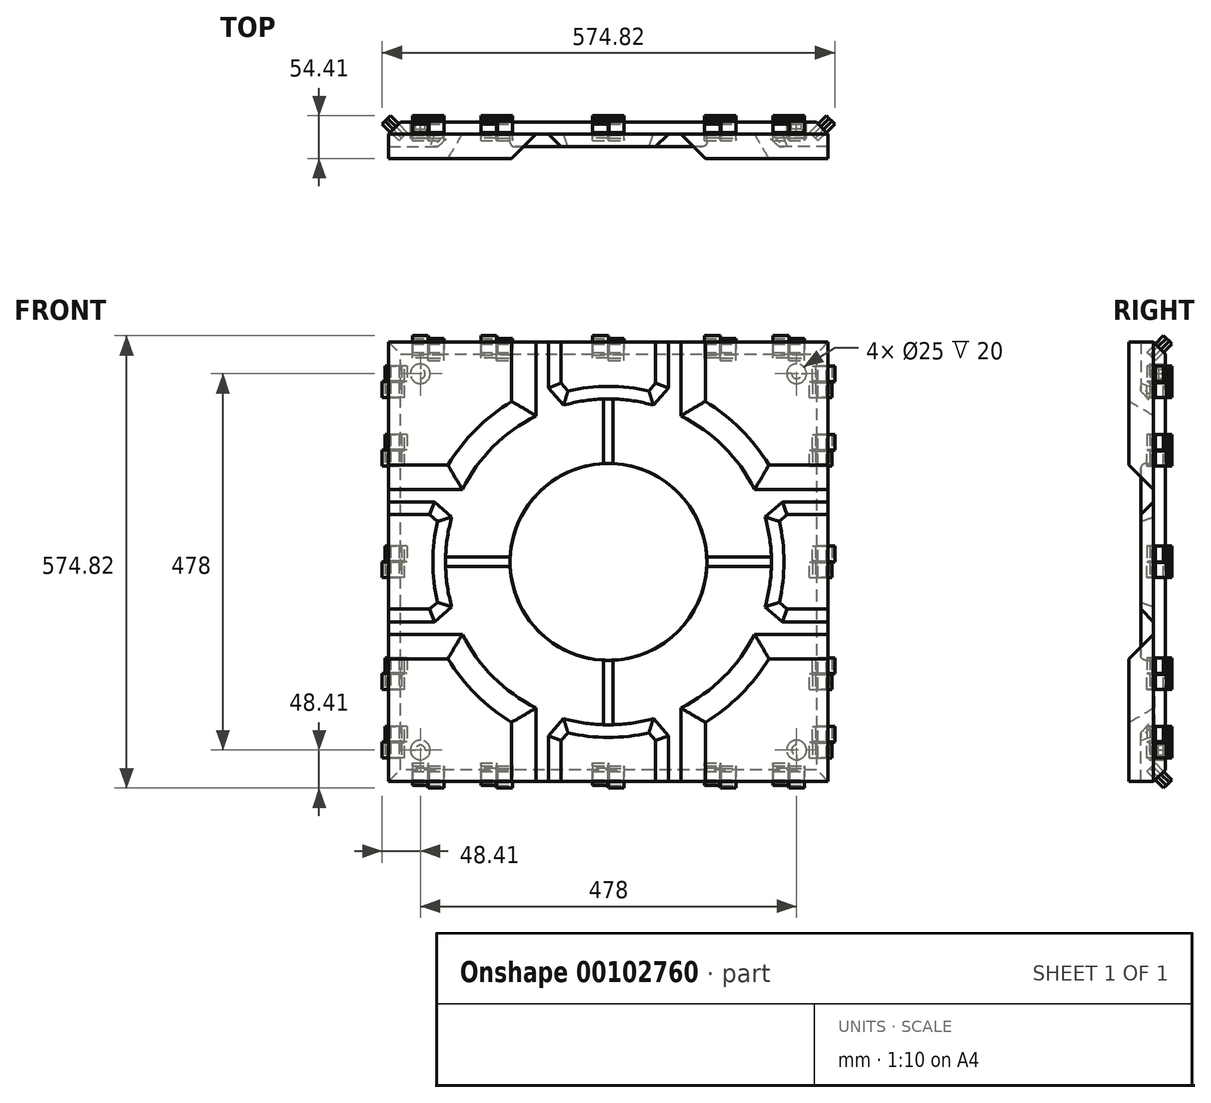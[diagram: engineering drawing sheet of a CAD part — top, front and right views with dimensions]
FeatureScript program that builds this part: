
annotation { "Feature Type Name" : "Feature", "Feature Type Description" : "" }
export const myFeature = defineFeature(function(context is Context, id is Id, definition is map)
    precondition{}
    {
        {
            var Q0;
            Q0=qCreatedBy(makeId("Front.planeOp"),FACE);
            var sketch = newSketch(context, id + "F0", { "sketchPlane" : qUnion([Q0])});
            skLineSegment(sketch, "E0.bottom", {"start": v(279, -279) * mm, "end": v(-279, -279) * mm});
            skLineSegment(sketch, "E0.top", {"start": v(279, 279) * mm, "end": v(-279, 279) * mm});
            skLineSegment(sketch, "E0.left", {"start": v(279, -279) * mm, "end": v(279, 279) * mm});
            skLineSegment(sketch, "E0.right", {"start": v(-279, -279) * mm, "end": v(-279, 279) * mm});
            skPoint(sketch, "E0.middle", {"position": v(0, 0) * mm});
            skCircle(sketch, "E1", {"center": v(0, 0) * mm, "radius": 125 * mm});
            skCircle(sketch, "E2", {"center": v(0, 0) * mm, "radius": 207 * mm});
            skLineSegment(sketch, "E3", {"start": v(-92, 279) * mm, "end": v(-92, 185.43) * mm});
            skLineSegment(sketch, "E4", {"start": v(-279, 92) * mm, "end": v(-185.43, 92) * mm});
            skLineSegment(sketch, "E5", {"start": v(92, 185.43) * mm, "end": v(92, 279) * mm});
            skLineSegment(sketch, "E6", {"start": v(185.43, 92) * mm, "end": v(279, 92) * mm});
            skLineSegment(sketch, "E7", {"start": v(92, -185.43) * mm, "end": v(92, -279) * mm});
            skLineSegment(sketch, "E8", {"start": v(-92, -185.43) * mm, "end": v(-92, -279) * mm});
            skLineSegment(sketch, "E9", {"start": v(-185.43, -92) * mm, "end": v(-279, -92) * mm});
            skLineSegment(sketch, "E10", {"start": v(185.43, -92) * mm, "end": v(279, -92) * mm});
            skLineSegment(sketch, "E11", {"start": v(-76, 279) * mm, "end": v(-76, 221) * mm});
            skLineSegment(sketch, "E12", {"start": v(76, 221) * mm, "end": v(76, 279) * mm});
            skLineSegment(sketch, "E13", {"start": v(-76, -221) * mm, "end": v(-76, -279) * mm});
            skLineSegment(sketch, "E14", {"start": v(76, -221) * mm, "end": v(76, -279) * mm});
            skLineSegment(sketch, "E15", {"start": v(-279, 76) * mm, "end": v(-221, 76) * mm});
            skLineSegment(sketch, "E16", {"start": v(-221, -76) * mm, "end": v(-279, -76) * mm});
            skLineSegment(sketch, "E17", {"start": v(221, 76) * mm, "end": v(279, 76) * mm});
            skLineSegment(sketch, "E18", {"start": v(221, -76) * mm, "end": v(279, -76) * mm});
            skLineSegment(sketch, "E19", {"start": v(-206.91, 6) * mm, "end": v(-124.86, 6) * mm});
            skLineSegment(sketch, "E20", {"start": v(-279, 0) * mm, "end": v(279, 0) * mm, "construction": true});
            skLineSegment(sketch, "E21", {"start": v(0, -279) * mm, "end": v(0, 279) * mm, "construction": true});
            skLineSegment(sketch, "E22", {"start": v(-206.91, -6) * mm, "end": v(-124.86, -6) * mm});
            skLineSegment(sketch, "E23", {"start": v(124.86, 6) * mm, "end": v(206.91, 6) * mm});
            skLineSegment(sketch, "E24", {"start": v(124.86, -6) * mm, "end": v(206.91, -6) * mm});
            skLineSegment(sketch, "E25", {"start": v(-6, 124.86) * mm, "end": v(-6, 206.91) * mm});
            skLineSegment(sketch, "E26", {"start": v(6, 206.91) * mm, "end": v(6, 124.86) * mm});
            skLineSegment(sketch, "E27", {"start": v(-6, -124.86) * mm, "end": v(-6, -206.91) * mm});
            skLineSegment(sketch, "E28", {"start": v(6, -124.86) * mm, "end": v(6, -206.91) * mm});
            skLineSegment(sketch, "E29", {"start": v(-199, 57) * mm, "end": v(-221, 76) * mm});
            skLineSegment(sketch, "E30", {"start": v(-199, -57) * mm, "end": v(-221, -76) * mm});
            skLineSegment(sketch, "E31", {"start": v(221, 76) * mm, "end": v(199, 57) * mm});
            skLineSegment(sketch, "E32", {"start": v(221, -76) * mm, "end": v(199, -57) * mm});
            skLineSegment(sketch, "E33", {"start": v(-76, 221) * mm, "end": v(-57, 199) * mm});
            skLineSegment(sketch, "E34", {"start": v(76, 221) * mm, "end": v(57, 199) * mm});
            skLineSegment(sketch, "E35", {"start": v(-57, -199) * mm, "end": v(-76, -221) * mm});
            skLineSegment(sketch, "E36", {"start": v(76, -221) * mm, "end": v(57, -199) * mm});
            skSolve(sketch);
        }
        {
            var Q0;
            Q0=qSketchRegion(id+"F0",true);
            var Q1;
            {var subQ3=sQuery(id+"F0.wireOp",EDGE,"E19");Q1=makeQuery(id+"F0.imprint","IMPRINT",FACE,{"disambiguationData":[TD([[makeQuery(id+"F0.imprint","IMPRINT",EDGE,{"derivedFrom":subQ3}),1.0]])]});}
            var Q2;
            {var subQ0=sQuery(id+"F0.wireOp",EDGE,"E25");Q2=makeQuery(id+"F0.imprint","IMPRINT",FACE,{"disambiguationData":[TD([[makeQuery(id+"F0.imprint","IMPRINT",EDGE,{"derivedFrom":subQ0}),-1.0]])]});}
            var Q3;
            {var subQ4=sQuery(id+"F0.wireOp",EDGE,"E23");Q3=makeQuery(id+"F0.imprint","IMPRINT",FACE,{"disambiguationData":[TD([[makeQuery(id+"F0.imprint","IMPRINT",EDGE,{"derivedFrom":subQ4}),1.0]])]});}
            var Q4;
            {var subQ0=sQuery(id+"F0.wireOp",EDGE,"E23");Q4=makeQuery(id+"F0.imprint","IMPRINT",FACE,{"disambiguationData":[TD([[makeQuery(id+"F0.imprint","IMPRINT",EDGE,{"derivedFrom":subQ0}),-1.0]])]});}
            var Q5;
            {var subQ5=sQuery(id+"F0.wireOp",EDGE,"E24");Q5=makeQuery(id+"F0.imprint","IMPRINT",FACE,{"disambiguationData":[TD([[makeQuery(id+"F0.imprint","IMPRINT",EDGE,{"derivedFrom":subQ5}),-1.0]])]});}
            var Q6;
            {var subQ0=sQuery(id+"F0.wireOp",EDGE,"E1");var subQ5=makeQuery(id+"F0.imprint","INTERSECT",VERTEX,{"derivedFrom":[subQ0,sQuery(id+"F0.wireOp",EDGE,"E23")]});Q6=makeQuery(id+"F0.imprint","IMPRINT",FACE,{"disambiguationData":[TD([[makeQuery(id+"F0.imprint","IMPRINT",EDGE,{"disambiguationData":[TD([[subQ5,-1.0]])],"derivedFrom":subQ0}),1.0]])]});}
            var Q7;
            {var subQ4=sQuery(id+"F0.wireOp",EDGE,"E22");Q7=makeQuery(id+"F0.imprint","IMPRINT",FACE,{"disambiguationData":[TD([[makeQuery(id+"F0.imprint","IMPRINT",EDGE,{"derivedFrom":subQ4}),-1.0]])]});}
            var Q8;
            {var subQ0=sQuery(id+"F0.wireOp",EDGE,"E27");Q8=makeQuery(id+"F0.imprint","IMPRINT",FACE,{"disambiguationData":[TD([[makeQuery(id+"F0.imprint","IMPRINT",EDGE,{"derivedFrom":subQ0}),1.0]])]});}
            var Q9;
            {var subQ0=sQuery(id+"F0.wireOp",EDGE,"E19");Q9=makeQuery(id+"F0.imprint","IMPRINT",FACE,{"disambiguationData":[TD([[makeQuery(id+"F0.imprint","IMPRINT",EDGE,{"derivedFrom":subQ0}),-1.0]])]});}
            extrude(context, id + "F1", {"entities" : qUnion([Q0, Q1, Q2, Q3, Q4, Q5, Q6, Q7, Q8, Q9]), "oppositeDirection" : true, "depth" : 15 * mm});
        }
        {
            var Q0;
            {var subQ0=sQuery(id+"F0.wireOp",EDGE,"E3");Q0=makeQuery(id+"F0.imprint","IMPRINT",FACE,{"disambiguationData":[TD([[makeQuery(id+"F0.imprint","IMPRINT",EDGE,{"derivedFrom":subQ0}),-1.0]])]});}
            var Q1;
            {var subQ0=sQuery(id+"F0.wireOp",EDGE,"E5");Q1=makeQuery(id+"F0.imprint","IMPRINT",FACE,{"disambiguationData":[TD([[makeQuery(id+"F0.imprint","IMPRINT",EDGE,{"derivedFrom":subQ0}),-1.0]])]});}
            var Q2;
            {var subQ0=sQuery(id+"F0.wireOp",EDGE,"E7");Q2=makeQuery(id+"F0.imprint","IMPRINT",FACE,{"disambiguationData":[TD([[makeQuery(id+"F0.imprint","IMPRINT",EDGE,{"derivedFrom":subQ0}),1.0]])]});}
            var Q3;
            {var subQ0=sQuery(id+"F0.wireOp",EDGE,"E8");Q3=makeQuery(id+"F0.imprint","IMPRINT",FACE,{"disambiguationData":[TD([[makeQuery(id+"F0.imprint","IMPRINT",EDGE,{"derivedFrom":subQ0}),-1.0]])]});}
            extrude(context, id + "F2", {"entities" : qUnion([Q0, Q1, Q2, Q3]), "operationType" : NewBodyOperationType.ADD, "depth" : 31 * mm});
        }
        {
            var Q0;
            {var subQ0=sQuery(id+"F0.wireOp",EDGE,"E2");Q0=makeQuery(id+"F2.opExtrude","CAP_EDGE",EDGE,{"disambiguationData":[OSD([subQ0]),TDD([makeQuery(id+"F0.imprint","IMPRINT",EDGE,{"disambiguationData":[TD([[makeQuery(id+"F0.imprint","INTERSECT",VERTEX,{"derivedFrom":[subQ0,sQuery(id+"F0.wireOp",EDGE,"E3")]}),-1.0]])],"derivedFrom":subQ0})])],"isStart":false});}
            var Q1;
            Q1=makeQuery(id+"F2.opExtrude","CAP_EDGE",EDGE,{"disambiguationData":[OSD([sQuery(id+"F0.wireOp",EDGE,"E4")])],"isStart":false});
            var Q2;
            Q2=makeQuery(id+"F2.opExtrude","CAP_EDGE",EDGE,{"disambiguationData":[OSD([sQuery(id+"F0.wireOp",EDGE,"E3")])],"isStart":false});
            var Q3;
            Q3=makeQuery(id+"F2.opExtrude","CAP_EDGE",EDGE,{"disambiguationData":[OSD([sQuery(id+"F0.wireOp",EDGE,"E5")])],"isStart":false});
            var Q4;
            {var subQ0=sQuery(id+"F0.wireOp",EDGE,"E2");Q4=makeQuery(id+"F2.opExtrude","CAP_EDGE",EDGE,{"disambiguationData":[OSD([subQ0]),TDD([makeQuery(id+"F0.imprint","IMPRINT",EDGE,{"disambiguationData":[TD([[makeQuery(id+"F0.imprint","INTERSECT",VERTEX,{"derivedFrom":[subQ0,sQuery(id+"F0.wireOp",EDGE,"E5")]}),1.0]])],"derivedFrom":subQ0})])],"isStart":false});}
            var Q5;
            Q5=makeQuery(id+"F2.opExtrude","CAP_EDGE",EDGE,{"disambiguationData":[OSD([sQuery(id+"F0.wireOp",EDGE,"E6")])],"isStart":false});
            var Q6;
            Q6=makeQuery(id+"F2.opExtrude","CAP_EDGE",EDGE,{"disambiguationData":[OSD([sQuery(id+"F0.wireOp",EDGE,"E10")])],"isStart":false});
            var Q7;
            {var subQ0=sQuery(id+"F0.wireOp",EDGE,"E2");Q7=makeQuery(id+"F2.opExtrude","CAP_EDGE",EDGE,{"disambiguationData":[OSD([subQ0]),TDD([makeQuery(id+"F0.imprint","IMPRINT",EDGE,{"disambiguationData":[TD([[makeQuery(id+"F0.imprint","INTERSECT",VERTEX,{"derivedFrom":[subQ0,sQuery(id+"F0.wireOp",EDGE,"E7")]}),-1.0]])],"derivedFrom":subQ0})])],"isStart":false});}
            var Q8;
            Q8=makeQuery(id+"F2.opExtrude","CAP_EDGE",EDGE,{"disambiguationData":[OSD([sQuery(id+"F0.wireOp",EDGE,"E7")])],"isStart":false});
            var Q9;
            Q9=makeQuery(id+"F2.opExtrude","CAP_EDGE",EDGE,{"disambiguationData":[OSD([sQuery(id+"F0.wireOp",EDGE,"E8")])],"isStart":false});
            var Q10;
            {var subQ0=sQuery(id+"F0.wireOp",EDGE,"E2");Q10=makeQuery(id+"F2.opExtrude","CAP_EDGE",EDGE,{"disambiguationData":[OSD([subQ0]),TDD([makeQuery(id+"F0.imprint","IMPRINT",EDGE,{"disambiguationData":[TD([[makeQuery(id+"F0.imprint","INTERSECT",VERTEX,{"derivedFrom":[subQ0,sQuery(id+"F0.wireOp",EDGE,"E8")]}),1.0]])],"derivedFrom":subQ0})])],"isStart":false});}
            var Q11;
            Q11=makeQuery(id+"F2.opExtrude","CAP_EDGE",EDGE,{"disambiguationData":[OSD([sQuery(id+"F0.wireOp",EDGE,"E9")])],"isStart":false});
            chamfer(context, id + "F3", {"entities" : qUnion([Q0, Q1, Q2, Q3, Q4, Q5, Q6, Q7, Q8, Q9, Q10, Q11]), "width" : 31 * mm, "tangentPropagation" : true});
        }
        {
            var Q0;
            {var subQ5=sQuery(id+"F0.wireOp",EDGE,"E15");Q0=makeQuery(id+"F0.imprint","IMPRINT",FACE,{"disambiguationData":[TD([[makeQuery(id+"F0.imprint","IMPRINT",EDGE,{"derivedFrom":subQ5}),-1.0]])]});}
            var Q1;
            {var subQ3=sQuery(id+"F0.wireOp",EDGE,"E11");Q1=makeQuery(id+"F0.imprint","IMPRINT",FACE,{"disambiguationData":[TD([[makeQuery(id+"F0.imprint","IMPRINT",EDGE,{"derivedFrom":subQ3}),1.0]])]});}
            var Q2;
            {var subQ0=sQuery(id+"F0.wireOp",EDGE,"E1");var subQ5=makeQuery(id+"F0.imprint","INTERSECT",VERTEX,{"derivedFrom":[subQ0,sQuery(id+"F0.wireOp",EDGE,"E23")]});Q2=makeQuery(id+"F0.imprint","IMPRINT",FACE,{"disambiguationData":[TD([[makeQuery(id+"F0.imprint","IMPRINT",EDGE,{"disambiguationData":[TD([[subQ5,-1.0]])],"derivedFrom":subQ0}),1.0]])]});}
            var Q3;
            {var subQ5=sQuery(id+"F0.wireOp",EDGE,"E17");Q3=makeQuery(id+"F0.imprint","IMPRINT",FACE,{"disambiguationData":[TD([[makeQuery(id+"F0.imprint","IMPRINT",EDGE,{"derivedFrom":subQ5}),-1.0]])]});}
            var Q4;
            {var subQ6=sQuery(id+"F0.wireOp",EDGE,"E13");Q4=makeQuery(id+"F0.imprint","IMPRINT",FACE,{"disambiguationData":[TD([[makeQuery(id+"F0.imprint","IMPRINT",EDGE,{"derivedFrom":subQ6}),1.0]])]});}
            extrude(context, id + "F4", {"entities" : qUnion([Q0, Q1, Q2, Q3, Q4]), "operationType" : NewBodyOperationType.ADD, "depth" : 16 * mm});
        }
        {
            var Q0;
            Q0=makeQuery(id+"F4.opExtrude","CAP_EDGE",EDGE,{"disambiguationData":[OSD([sQuery(id+"F0.wireOp",EDGE,"E15")])],"isStart":false});
            var Q1;
            Q1=makeQuery(id+"F4.opExtrude","CAP_EDGE",EDGE,{"disambiguationData":[OSD([sQuery(id+"F0.wireOp",EDGE,"E29")])],"isStart":false});
            var Q2;
            {var subQ0=sQuery(id+"F0.wireOp",EDGE,"E2");var subQ1=makeQuery(id+"F0.imprint","INTERSECT",VERTEX,{"derivedFrom":[subQ0,sQuery(id+"F0.wireOp",EDGE,"E22")]});var subQ2=makeQuery(id+"F0.imprint","INTERSECT",VERTEX,{"derivedFrom":[subQ0,sQuery(id+"F0.wireOp",EDGE,"E19")]});Q2=makeQuery(id+"F4.opExtrude","CAP_EDGE",EDGE,{"disambiguationData":[OSD([subQ0]),TDD([makeQuery(id+"F0.imprint","IMPRINT",EDGE,{"disambiguationData":[TD([[subQ2,1.0]])],"derivedFrom":subQ0}),makeQuery(id+"F0.imprint","IMPRINT",EDGE,{"disambiguationData":[TD([[subQ2,-1.0]])],"derivedFrom":subQ0}),makeQuery(id+"F0.imprint","IMPRINT",EDGE,{"disambiguationData":[TD([[subQ1,-1.0]])],"derivedFrom":subQ0})])],"isStart":false});}
            var Q3;
            Q3=makeQuery(id+"F4.opExtrude","CAP_EDGE",EDGE,{"disambiguationData":[OSD([sQuery(id+"F0.wireOp",EDGE,"E30")])],"isStart":false});
            var Q4;
            Q4=makeQuery(id+"F4.opExtrude","CAP_EDGE",EDGE,{"disambiguationData":[OSD([sQuery(id+"F0.wireOp",EDGE,"E16")])],"isStart":false});
            var Q5;
            Q5=makeQuery(id+"F4.opExtrude","CAP_EDGE",EDGE,{"disambiguationData":[OSD([sQuery(id+"F0.wireOp",EDGE,"E13")])],"isStart":false});
            var Q6;
            Q6=makeQuery(id+"F4.opExtrude","CAP_EDGE",EDGE,{"disambiguationData":[OSD([sQuery(id+"F0.wireOp",EDGE,"E35")])],"isStart":false});
            var Q7;
            {var subQ0=sQuery(id+"F0.wireOp",EDGE,"E2");var subQ1=makeQuery(id+"F0.imprint","INTERSECT",VERTEX,{"derivedFrom":[subQ0,sQuery(id+"F0.wireOp",EDGE,"E28")]});var subQ2=makeQuery(id+"F0.imprint","INTERSECT",VERTEX,{"derivedFrom":[subQ0,sQuery(id+"F0.wireOp",EDGE,"E27")]});Q7=makeQuery(id+"F4.opExtrude","CAP_EDGE",EDGE,{"disambiguationData":[OSD([subQ0]),TDD([makeQuery(id+"F0.imprint","IMPRINT",EDGE,{"disambiguationData":[TD([[subQ2,1.0]])],"derivedFrom":subQ0}),makeQuery(id+"F0.imprint","IMPRINT",EDGE,{"disambiguationData":[TD([[subQ2,-1.0]])],"derivedFrom":subQ0}),makeQuery(id+"F0.imprint","IMPRINT",EDGE,{"disambiguationData":[TD([[subQ1,-1.0]])],"derivedFrom":subQ0})])],"isStart":false});}
            var Q8;
            Q8=makeQuery(id+"F4.opExtrude","CAP_EDGE",EDGE,{"disambiguationData":[OSD([sQuery(id+"F0.wireOp",EDGE,"E36")])],"isStart":false});
            var Q9;
            Q9=makeQuery(id+"F4.opExtrude","CAP_EDGE",EDGE,{"disambiguationData":[OSD([sQuery(id+"F0.wireOp",EDGE,"E14")])],"isStart":false});
            var Q10;
            Q10=makeQuery(id+"F4.opExtrude","CAP_EDGE",EDGE,{"disambiguationData":[OSD([sQuery(id+"F0.wireOp",EDGE,"E18")])],"isStart":false});
            var Q11;
            Q11=makeQuery(id+"F4.opExtrude","CAP_EDGE",EDGE,{"disambiguationData":[OSD([sQuery(id+"F0.wireOp",EDGE,"E32")])],"isStart":false});
            var Q12;
            {var subQ0=sQuery(id+"F0.wireOp",EDGE,"E2");var subQ1=makeQuery(id+"F0.imprint","INTERSECT",VERTEX,{"derivedFrom":[subQ0,sQuery(id+"F0.wireOp",EDGE,"E23")]});var subQ2=makeQuery(id+"F0.imprint","INTERSECT",VERTEX,{"derivedFrom":[subQ0,sQuery(id+"F0.wireOp",EDGE,"E24")]});Q12=makeQuery(id+"F4.opExtrude","CAP_EDGE",EDGE,{"disambiguationData":[OSD([subQ0]),TDD([makeQuery(id+"F0.imprint","IMPRINT",EDGE,{"disambiguationData":[TD([[subQ1,-1.0]])],"derivedFrom":subQ0}),makeQuery(id+"F0.imprint","IMPRINT",EDGE,{"disambiguationData":[TD([[subQ2,1.0]])],"derivedFrom":subQ0}),makeQuery(id+"F0.imprint","IMPRINT",EDGE,{"disambiguationData":[TD([[subQ1,1.0]])],"derivedFrom":subQ0})])],"isStart":false});}
            var Q13;
            Q13=makeQuery(id+"F4.opExtrude","CAP_EDGE",EDGE,{"disambiguationData":[OSD([sQuery(id+"F0.wireOp",EDGE,"E31")])],"isStart":false});
            var Q14;
            Q14=makeQuery(id+"F4.opExtrude","CAP_EDGE",EDGE,{"disambiguationData":[OSD([sQuery(id+"F0.wireOp",EDGE,"E17")])],"isStart":false});
            var Q15;
            Q15=makeQuery(id+"F4.opExtrude","CAP_EDGE",EDGE,{"disambiguationData":[OSD([sQuery(id+"F0.wireOp",EDGE,"E12")])],"isStart":false});
            var Q16;
            Q16=makeQuery(id+"F4.opExtrude","CAP_EDGE",EDGE,{"disambiguationData":[OSD([sQuery(id+"F0.wireOp",EDGE,"E34")])],"isStart":false});
            var Q17;
            {var subQ0=sQuery(id+"F0.wireOp",EDGE,"E2");var subQ1=makeQuery(id+"F0.imprint","INTERSECT",VERTEX,{"derivedFrom":[subQ0,sQuery(id+"F0.wireOp",EDGE,"E25")]});var subQ2=makeQuery(id+"F0.imprint","INTERSECT",VERTEX,{"derivedFrom":[subQ0,sQuery(id+"F0.wireOp",EDGE,"E26")]});Q17=makeQuery(id+"F4.opExtrude","CAP_EDGE",EDGE,{"disambiguationData":[OSD([subQ0]),TDD([makeQuery(id+"F0.imprint","IMPRINT",EDGE,{"disambiguationData":[TD([[subQ2,1.0]])],"derivedFrom":subQ0}),makeQuery(id+"F0.imprint","IMPRINT",EDGE,{"disambiguationData":[TD([[subQ1,1.0]])],"derivedFrom":subQ0}),makeQuery(id+"F0.imprint","IMPRINT",EDGE,{"disambiguationData":[TD([[subQ1,-1.0]])],"derivedFrom":subQ0})])],"isStart":false});}
            var Q18;
            Q18=makeQuery(id+"F4.opExtrude","CAP_EDGE",EDGE,{"disambiguationData":[OSD([sQuery(id+"F0.wireOp",EDGE,"E33")])],"isStart":false});
            var Q19;
            Q19=makeQuery(id+"F4.opExtrude","CAP_EDGE",EDGE,{"disambiguationData":[OSD([sQuery(id+"F0.wireOp",EDGE,"E11")])],"isStart":false});
            chamfer(context, id + "F5", {"entities" : qUnion([Q0, Q1, Q2, Q3, Q4, Q5, Q6, Q7, Q8, Q9, Q10, Q11, Q12, Q13, Q14, Q15, Q16, Q17, Q18, Q19]), "width" : 16 * mm, "tangentPropagation" : true});
        }
        {
            var Q0;
            Q0=makeQuery(id+"F4.opExtrude","CAP_EDGE",EDGE,{"disambiguationData":[OSD([sQuery(id+"F0.wireOp",EDGE,"E1")])],"isStart":false});
            fillet(context, id + "F6", {"entities" : qUnion([Q0]), "radius" : 6 * mm, "tangentPropagation" : true, "allowEdgeOverflow" : false});
        }
        {
            var Q0;
            Q0=makeQuery(id+"F1.opExtrude","CAP_FACE",FACE,{"disambiguationData":[OSD([sQuery(id+"F0.wireOp",EDGE,"E0.bottom"),sQuery(id+"F0.wireOp",EDGE,"E0.top"),sQuery(id+"F0.wireOp",EDGE,"E0.left"),sQuery(id+"F0.wireOp",EDGE,"E0.right")])],"isStart":false});
            chamfer(context, id + "F7", {"entities" : qUnion([Q0]), "width" : 15 * mm, "tangentPropagation" : true});
        }
        {
            var Q0;
            {var subQ0=sQuery(id+"F0.wireOp",EDGE,"E19");Q0=makeQuery(id+"F0.imprint","IMPRINT",FACE,{"disambiguationData":[TD([[makeQuery(id+"F0.imprint","IMPRINT",EDGE,{"derivedFrom":subQ0}),-1.0]])]});}
            var Q1;
            {var subQ0=sQuery(id+"F0.wireOp",EDGE,"E25");Q1=makeQuery(id+"F0.imprint","IMPRINT",FACE,{"disambiguationData":[TD([[makeQuery(id+"F0.imprint","IMPRINT",EDGE,{"derivedFrom":subQ0}),-1.0]])]});}
            var Q2;
            {var subQ0=sQuery(id+"F0.wireOp",EDGE,"E23");Q2=makeQuery(id+"F0.imprint","IMPRINT",FACE,{"disambiguationData":[TD([[makeQuery(id+"F0.imprint","IMPRINT",EDGE,{"derivedFrom":subQ0}),-1.0]])]});}
            var Q3;
            {var subQ0=sQuery(id+"F0.wireOp",EDGE,"E27");Q3=makeQuery(id+"F0.imprint","IMPRINT",FACE,{"disambiguationData":[TD([[makeQuery(id+"F0.imprint","IMPRINT",EDGE,{"derivedFrom":subQ0}),1.0]])]});}
            extrude(context, id + "F8", {"entities" : qUnion([Q0, Q1, Q2, Q3]), "operationType" : NewBodyOperationType.REMOVE, "oppositeDirection" : true, "depth" : 1 * mm});
        }
        {
            var Q0;
            Q0=makeQuery(id+"F7.opChamfer","BLEND_FACE",FACE,{"disambiguationData":[OSD([sQuery(id+"F0.wireOp",EDGE,"E0.right")])]});
            var sketch = newSketch(context, id + "F9", { "sketchPlane" : qUnion([Q0])});
            skLineSegment(sketch, "E37.0", {"start": v(176.07, -264) * mm, "end": v(176.07, 264) * mm});
            skLineSegment(sketch, "E38.0", {"start": v(197.28, 76) * mm, "end": v(197.28, -76) * mm});
            skLineSegment(sketch, "E39.0", {"start": v(197.28, -92) * mm, "end": v(197.28, -279) * mm});
            skLineSegment(sketch, "E40.0", {"start": v(197.28, -92) * mm, "end": v(197.28, -76) * mm});
            skLineSegment(sketch, "E41.0", {"start": v(197.28, 76) * mm, "end": v(197.28, 92) * mm});
            skLineSegment(sketch, "E41.1", {"start": v(197.28, 279) * mm, "end": v(197.28, 92) * mm});
            skLineSegment(sketch, "E41.2", {"start": v(197.28, 279) * mm, "end": v(176.07, 264) * mm});
            skLineSegment(sketch, "E41.3", {"start": v(176.07, -264) * mm, "end": v(197.28, -279) * mm});
            skLineSegment(sketch, "E42", {"start": v(176.07, -263.86) * mm, "end": v(197.28, -263.86) * mm, "construction": true});
            skLineSegment(sketch, "E43", {"start": v(186.68, 267.3) * mm, "end": v(186.68, -263.86) * mm, "construction": true});
            skPoint(sketch, "E44.middle", {"position": v(186.68, 229) * mm});
            skLineSegment(sketch, "E45.bottom", {"start": v(179.18, 249) * mm, "end": v(194.18, 249) * mm});
            skLineSegment(sketch, "E45.top", {"start": v(179.18, 209) * mm, "end": v(194.18, 209) * mm});
            skLineSegment(sketch, "E45.left", {"start": v(179.18, 249) * mm, "end": v(179.18, 209) * mm});
            skLineSegment(sketch, "E45.right", {"start": v(194.18, 249) * mm, "end": v(194.18, 209) * mm});
            skLineSegment(sketch, "E46.MirrorCS", {"start": v(189.18, 249) * mm, "end": v(189.18, 230) * mm});
            skLineSegment(sketch, "E47", {"start": v(184.18, 209) * mm, "end": v(184.18, 228) * mm});
            skLineSegment(sketch, "E48.trimOffspring", {"start": v(184.18, 230) * mm, "end": v(184.18, 249) * mm});
            skLineSegment(sketch, "E49.trimOffspring", {"start": v(189.18, 228) * mm, "end": v(189.18, 209) * mm});
            skLineSegment(sketch, "E50", {"start": v(179.18, 229) * mm, "end": v(184.18, 230) * mm});
            skLineSegment(sketch, "E51", {"start": v(189.18, 230) * mm, "end": v(194.18, 229) * mm});
            skLineSegment(sketch, "E52", {"start": v(184.18, 228) * mm, "end": v(189.18, 228) * mm});
            skPoint(sketch, "E53.middle", {"position": v(186.68, 142) * mm});
            skLineSegment(sketch, "E54.bottom", {"start": v(179.18, 162) * mm, "end": v(194.18, 162) * mm});
            skLineSegment(sketch, "E54.top", {"start": v(179.18, 122) * mm, "end": v(194.18, 122) * mm});
            skLineSegment(sketch, "E54.left", {"start": v(179.18, 162) * mm, "end": v(179.18, 122) * mm});
            skLineSegment(sketch, "E54.right", {"start": v(194.18, 162) * mm, "end": v(194.18, 122) * mm});
            skLineSegment(sketch, "E55.MirrorCS", {"start": v(189.18, 162) * mm, "end": v(189.18, 143) * mm});
            skLineSegment(sketch, "E56", {"start": v(184.18, 122) * mm, "end": v(184.18, 141) * mm});
            skLineSegment(sketch, "E57.trimOffspring", {"start": v(184.18, 143) * mm, "end": v(184.18, 162) * mm});
            skLineSegment(sketch, "E58.trimOffspring", {"start": v(189.18, 141) * mm, "end": v(189.18, 122) * mm});
            skLineSegment(sketch, "E59", {"start": v(179.18, 142) * mm, "end": v(184.18, 143) * mm});
            skLineSegment(sketch, "E60", {"start": v(189.18, 143) * mm, "end": v(194.18, 142) * mm});
            skLineSegment(sketch, "E61", {"start": v(184.18, 141) * mm, "end": v(189.18, 141) * mm});
            skPoint(sketch, "E62.middle", {"position": v(186.68, 0) * mm});
            skLineSegment(sketch, "E63.bottom", {"start": v(179.18, 20) * mm, "end": v(194.18, 20) * mm});
            skLineSegment(sketch, "E63.top", {"start": v(179.18, -20) * mm, "end": v(194.18, -20) * mm});
            skLineSegment(sketch, "E63.left", {"start": v(179.18, 20) * mm, "end": v(179.18, -20) * mm});
            skLineSegment(sketch, "E63.right", {"start": v(194.18, 20) * mm, "end": v(194.18, -20) * mm});
            skLineSegment(sketch, "E64.MirrorCS", {"start": v(189.18, 20) * mm, "end": v(189.18, 1) * mm});
            skLineSegment(sketch, "E65", {"start": v(184.18, -20) * mm, "end": v(184.18, -1) * mm});
            skLineSegment(sketch, "E66.trimOffspring", {"start": v(184.18, 1) * mm, "end": v(184.18, 20) * mm});
            skLineSegment(sketch, "E67.trimOffspring", {"start": v(189.18, -1) * mm, "end": v(189.18, -20) * mm});
            skLineSegment(sketch, "E68", {"start": v(179.18, 0) * mm, "end": v(184.18, 1) * mm});
            skLineSegment(sketch, "E69", {"start": v(189.18, 1) * mm, "end": v(194.18, 0) * mm});
            skLineSegment(sketch, "E70", {"start": v(184.18, -1) * mm, "end": v(189.18, -1) * mm});
            skPoint(sketch, "E71.middle", {"position": v(186.68, -229) * mm});
            skLineSegment(sketch, "E72.bottom", {"start": v(179.18, -209) * mm, "end": v(194.18, -209) * mm});
            skLineSegment(sketch, "E72.top", {"start": v(179.18, -249) * mm, "end": v(194.18, -249) * mm});
            skLineSegment(sketch, "E72.left", {"start": v(179.18, -209) * mm, "end": v(179.18, -249) * mm});
            skLineSegment(sketch, "E72.right", {"start": v(194.18, -209) * mm, "end": v(194.18, -249) * mm});
            skLineSegment(sketch, "E73.MirrorCS", {"start": v(189.18, -209) * mm, "end": v(189.18, -228) * mm});
            skLineSegment(sketch, "E74", {"start": v(184.18, -249) * mm, "end": v(184.18, -230) * mm});
            skLineSegment(sketch, "E75.trimOffspring", {"start": v(184.18, -228) * mm, "end": v(184.18, -209) * mm});
            skLineSegment(sketch, "E76.trimOffspring", {"start": v(189.18, -230) * mm, "end": v(189.18, -249) * mm});
            skLineSegment(sketch, "E77", {"start": v(179.18, -229) * mm, "end": v(184.18, -228) * mm});
            skLineSegment(sketch, "E78", {"start": v(189.18, -228) * mm, "end": v(194.18, -229) * mm});
            skLineSegment(sketch, "E79", {"start": v(184.18, -230) * mm, "end": v(189.18, -230) * mm});
            skPoint(sketch, "E80.middle", {"position": v(186.68, -142) * mm});
            skLineSegment(sketch, "E81.bottom", {"start": v(179.18, -122) * mm, "end": v(194.18, -122) * mm});
            skLineSegment(sketch, "E81.top", {"start": v(179.18, -162) * mm, "end": v(194.18, -162) * mm});
            skLineSegment(sketch, "E81.left", {"start": v(179.18, -122) * mm, "end": v(179.18, -162) * mm});
            skLineSegment(sketch, "E81.right", {"start": v(194.18, -122) * mm, "end": v(194.18, -162) * mm});
            skLineSegment(sketch, "E82.MirrorCS", {"start": v(189.18, -122) * mm, "end": v(189.18, -141) * mm});
            skLineSegment(sketch, "E83", {"start": v(184.18, -162) * mm, "end": v(184.18, -143) * mm});
            skLineSegment(sketch, "E84.trimOffspring", {"start": v(184.18, -141) * mm, "end": v(184.18, -122) * mm});
            skLineSegment(sketch, "E85.trimOffspring", {"start": v(189.18, -143) * mm, "end": v(189.18, -162) * mm});
            skLineSegment(sketch, "E86", {"start": v(179.18, -142) * mm, "end": v(184.18, -141) * mm});
            skLineSegment(sketch, "E87", {"start": v(189.18, -141) * mm, "end": v(194.18, -142) * mm});
            skLineSegment(sketch, "E88", {"start": v(184.18, -143) * mm, "end": v(189.18, -143) * mm});
            skSolve(sketch);
        }
        {
            var Q0;
            {var subQ3=sQuery(id+"F9.wireOp",EDGE,"E48.trimOffspring");Q0=makeQuery(id+"F9.imprint","IMPRINT",FACE,{"disambiguationData":[TD([[makeQuery(id+"F9.imprint","IMPRINT",EDGE,{"derivedFrom":subQ3}),1.0]])]});}
            var Q1;
            {var subQ0=sQuery(id+"F9.wireOp",EDGE,"E47");Q1=makeQuery(id+"F9.imprint","IMPRINT",FACE,{"disambiguationData":[TD([[makeQuery(id+"F9.imprint","IMPRINT",EDGE,{"derivedFrom":subQ0}),-1.0]])]});}
            var Q2;
            {var subQ3=sQuery(id+"F9.wireOp",EDGE,"E46.MirrorCS");Q2=makeQuery(id+"F9.imprint","IMPRINT",FACE,{"disambiguationData":[TD([[makeQuery(id+"F9.imprint","IMPRINT",EDGE,{"derivedFrom":subQ3}),1.0]])]});}
            var Q3;
            {var subQ3=sQuery(id+"F9.wireOp",EDGE,"E57.trimOffspring");Q3=makeQuery(id+"F9.imprint","IMPRINT",FACE,{"disambiguationData":[TD([[makeQuery(id+"F9.imprint","IMPRINT",EDGE,{"derivedFrom":subQ3}),1.0]])]});}
            var Q4;
            {var subQ3=sQuery(id+"F9.wireOp",EDGE,"E55.MirrorCS");Q4=makeQuery(id+"F9.imprint","IMPRINT",FACE,{"disambiguationData":[TD([[makeQuery(id+"F9.imprint","IMPRINT",EDGE,{"derivedFrom":subQ3}),1.0]])]});}
            var Q5;
            {var subQ0=sQuery(id+"F9.wireOp",EDGE,"E56");Q5=makeQuery(id+"F9.imprint","IMPRINT",FACE,{"disambiguationData":[TD([[makeQuery(id+"F9.imprint","IMPRINT",EDGE,{"derivedFrom":subQ0}),-1.0]])]});}
            var Q6;
            {var subQ3=sQuery(id+"F9.wireOp",EDGE,"E66.trimOffspring");Q6=makeQuery(id+"F9.imprint","IMPRINT",FACE,{"disambiguationData":[TD([[makeQuery(id+"F9.imprint","IMPRINT",EDGE,{"derivedFrom":subQ3}),1.0]])]});}
            var Q7;
            {var subQ0=sQuery(id+"F9.wireOp",EDGE,"E65");Q7=makeQuery(id+"F9.imprint","IMPRINT",FACE,{"disambiguationData":[TD([[makeQuery(id+"F9.imprint","IMPRINT",EDGE,{"derivedFrom":subQ0}),-1.0]])]});}
            var Q8;
            {var subQ3=sQuery(id+"F9.wireOp",EDGE,"E64.MirrorCS");Q8=makeQuery(id+"F9.imprint","IMPRINT",FACE,{"disambiguationData":[TD([[makeQuery(id+"F9.imprint","IMPRINT",EDGE,{"derivedFrom":subQ3}),1.0]])]});}
            var Q9;
            {var subQ3=sQuery(id+"F9.wireOp",EDGE,"E84.trimOffspring");Q9=makeQuery(id+"F9.imprint","IMPRINT",FACE,{"disambiguationData":[TD([[makeQuery(id+"F9.imprint","IMPRINT",EDGE,{"derivedFrom":subQ3}),1.0]])]});}
            var Q10;
            {var subQ0=sQuery(id+"F9.wireOp",EDGE,"E83");Q10=makeQuery(id+"F9.imprint","IMPRINT",FACE,{"disambiguationData":[TD([[makeQuery(id+"F9.imprint","IMPRINT",EDGE,{"derivedFrom":subQ0}),-1.0]])]});}
            var Q11;
            {var subQ3=sQuery(id+"F9.wireOp",EDGE,"E82.MirrorCS");Q11=makeQuery(id+"F9.imprint","IMPRINT",FACE,{"disambiguationData":[TD([[makeQuery(id+"F9.imprint","IMPRINT",EDGE,{"derivedFrom":subQ3}),1.0]])]});}
            var Q12;
            {var subQ3=sQuery(id+"F9.wireOp",EDGE,"E75.trimOffspring");Q12=makeQuery(id+"F9.imprint","IMPRINT",FACE,{"disambiguationData":[TD([[makeQuery(id+"F9.imprint","IMPRINT",EDGE,{"derivedFrom":subQ3}),1.0]])]});}
            var Q13;
            {var subQ0=sQuery(id+"F9.wireOp",EDGE,"E74");Q13=makeQuery(id+"F9.imprint","IMPRINT",FACE,{"disambiguationData":[TD([[makeQuery(id+"F9.imprint","IMPRINT",EDGE,{"derivedFrom":subQ0}),-1.0]])]});}
            var Q14;
            {var subQ3=sQuery(id+"F9.wireOp",EDGE,"E73.MirrorCS");Q14=makeQuery(id+"F9.imprint","IMPRINT",FACE,{"disambiguationData":[TD([[makeQuery(id+"F9.imprint","IMPRINT",EDGE,{"derivedFrom":subQ3}),1.0]])]});}
            extrude(context, id + "F10", {"entities" : qUnion([Q0, Q1, Q2, Q3, Q4, Q5, Q6, Q7, Q8, Q9, Q10, Q11, Q12, Q13, Q14]), "operationType" : NewBodyOperationType.REMOVE, "oppositeDirection" : true, "depth" : 15 * mm});
        }
        {
            var Q0;
            {var subQ1=sQuery(id+"F9.wireOp",EDGE,"E73.MirrorCS");Q0=makeQuery(id+"F9.imprint","IMPRINT",FACE,{"disambiguationData":[TD([[makeQuery(id+"F9.imprint","IMPRINT",EDGE,{"derivedFrom":subQ1}),-1.0]])]});}
            var Q1;
            {var subQ2=sQuery(id+"F9.wireOp",EDGE,"E82.MirrorCS");Q1=makeQuery(id+"F9.imprint","IMPRINT",FACE,{"disambiguationData":[TD([[makeQuery(id+"F9.imprint","IMPRINT",EDGE,{"derivedFrom":subQ2}),-1.0]])]});}
            var Q2;
            {var subQ8=sQuery(id+"F9.wireOp",EDGE,"E64.MirrorCS");Q2=makeQuery(id+"F9.imprint","IMPRINT",FACE,{"disambiguationData":[TD([[makeQuery(id+"F9.imprint","IMPRINT",EDGE,{"derivedFrom":subQ8}),-1.0]])]});}
            var Q3;
            {var subQ4=sQuery(id+"F9.wireOp",EDGE,"E55.MirrorCS");Q3=makeQuery(id+"F9.imprint","IMPRINT",FACE,{"disambiguationData":[TD([[makeQuery(id+"F9.imprint","IMPRINT",EDGE,{"derivedFrom":subQ4}),-1.0]])]});}
            var Q4;
            {var subQ1=sQuery(id+"F9.wireOp",EDGE,"E46.MirrorCS");Q4=makeQuery(id+"F9.imprint","IMPRINT",FACE,{"disambiguationData":[TD([[makeQuery(id+"F9.imprint","IMPRINT",EDGE,{"derivedFrom":subQ1}),-1.0]])]});}
            extrude(context, id + "F11", {"entities" : qUnion([Q0, Q1, Q2, Q3, Q4]), "operationType" : NewBodyOperationType.ADD, "depth" : 15 * mm});
        }
        {
            var Q0;
            Q0=makeQuery(id+"F7.opChamfer","BLEND_FACE",FACE,{"disambiguationData":[OSD([sQuery(id+"F0.wireOp",EDGE,"E0.left")])]});
            var sketch = newSketch(context, id + "F12", { "sketchPlane" : qUnion([Q0])});
            skLineSegment(sketch, "E89", {"start": v(-197.28, -257.71) * mm, "end": v(-176.07, -257.71) * mm, "construction": true});
            skLineSegment(sketch, "E90", {"start": v(-186.68, -257.71) * mm, "end": v(-186.68, 257.71) * mm, "construction": true});
            skLineSegment(sketch, "E91.bottom", {"start": v(-179.18, 209) * mm, "end": v(-194.18, 209) * mm});
            skLineSegment(sketch, "E91.top", {"start": v(-179.18, 249) * mm, "end": v(-194.18, 249) * mm});
            skLineSegment(sketch, "E91.left", {"start": v(-179.18, 209) * mm, "end": v(-179.18, 249) * mm});
            skLineSegment(sketch, "E91.right", {"start": v(-194.18, 209) * mm, "end": v(-194.18, 249) * mm});
            skPoint(sketch, "E91.middle", {"position": v(-186.68, 229) * mm});
            skLineSegment(sketch, "E92", {"start": v(-189.18, 249) * mm, "end": v(-189.18, 230) * mm});
            skLineSegment(sketch, "E93", {"start": v(-189.18, 230) * mm, "end": v(-184.18, 230) * mm});
            skLineSegment(sketch, "E94", {"start": v(-184.18, 230) * mm, "end": v(-184.18, 249) * mm});
            skLineSegment(sketch, "E95", {"start": v(-194.18, 229) * mm, "end": v(-189.18, 228) * mm});
            skLineSegment(sketch, "E96", {"start": v(-189.18, 228) * mm, "end": v(-189.18, 209) * mm});
            skLineSegment(sketch, "E97", {"start": v(-179.18, 229) * mm, "end": v(-184.18, 228) * mm});
            skLineSegment(sketch, "E98", {"start": v(-184.18, 228) * mm, "end": v(-184.18, 209) * mm});
            skLineSegment(sketch, "E99.bottom", {"start": v(-179.18, 122) * mm, "end": v(-194.18, 122) * mm});
            skLineSegment(sketch, "E99.top", {"start": v(-179.18, 162) * mm, "end": v(-194.18, 162) * mm});
            skLineSegment(sketch, "E99.left", {"start": v(-179.18, 122) * mm, "end": v(-179.18, 162) * mm});
            skLineSegment(sketch, "E99.right", {"start": v(-194.18, 122) * mm, "end": v(-194.18, 162) * mm});
            skPoint(sketch, "E99.middle", {"position": v(-186.68, 142) * mm});
            skLineSegment(sketch, "E100", {"start": v(-189.18, 162) * mm, "end": v(-189.18, 143) * mm});
            skLineSegment(sketch, "E101", {"start": v(-189.18, 143) * mm, "end": v(-184.18, 143) * mm});
            skLineSegment(sketch, "E102", {"start": v(-184.18, 143) * mm, "end": v(-184.18, 162) * mm});
            skLineSegment(sketch, "E103", {"start": v(-194.18, 142) * mm, "end": v(-189.18, 141) * mm});
            skLineSegment(sketch, "E104", {"start": v(-189.18, 141) * mm, "end": v(-189.18, 122) * mm});
            skLineSegment(sketch, "E105", {"start": v(-179.18, 142) * mm, "end": v(-184.18, 141) * mm});
            skLineSegment(sketch, "E106", {"start": v(-184.18, 141) * mm, "end": v(-184.18, 122) * mm});
            skLineSegment(sketch, "E107.bottom", {"start": v(-179.18, -20) * mm, "end": v(-194.18, -20) * mm});
            skLineSegment(sketch, "E107.top", {"start": v(-179.18, 20) * mm, "end": v(-194.18, 20) * mm});
            skLineSegment(sketch, "E107.left", {"start": v(-179.18, -20) * mm, "end": v(-179.18, 20) * mm});
            skLineSegment(sketch, "E107.right", {"start": v(-194.18, -20) * mm, "end": v(-194.18, 20) * mm});
            skPoint(sketch, "E107.middle", {"position": v(-186.68, 0) * mm});
            skLineSegment(sketch, "E108", {"start": v(-189.18, 20) * mm, "end": v(-189.18, 1) * mm});
            skLineSegment(sketch, "E109", {"start": v(-189.18, 1) * mm, "end": v(-184.18, 1) * mm});
            skLineSegment(sketch, "E110", {"start": v(-184.18, 1) * mm, "end": v(-184.18, 20) * mm});
            skLineSegment(sketch, "E111", {"start": v(-194.18, 0) * mm, "end": v(-189.18, -1) * mm});
            skLineSegment(sketch, "E112", {"start": v(-189.18, -1) * mm, "end": v(-189.18, -20) * mm});
            skLineSegment(sketch, "E113", {"start": v(-179.18, 0) * mm, "end": v(-184.18, -1) * mm});
            skLineSegment(sketch, "E114", {"start": v(-184.18, -1) * mm, "end": v(-184.18, -20) * mm});
            skLineSegment(sketch, "E115.bottom", {"start": v(-179.18, -162) * mm, "end": v(-194.18, -162) * mm});
            skLineSegment(sketch, "E115.top", {"start": v(-179.18, -122) * mm, "end": v(-194.18, -122) * mm});
            skLineSegment(sketch, "E115.left", {"start": v(-179.18, -162) * mm, "end": v(-179.18, -122) * mm});
            skLineSegment(sketch, "E115.right", {"start": v(-194.18, -162) * mm, "end": v(-194.18, -122) * mm});
            skPoint(sketch, "E115.middle", {"position": v(-186.68, -142) * mm});
            skLineSegment(sketch, "E116", {"start": v(-189.18, -122) * mm, "end": v(-189.18, -141) * mm});
            skLineSegment(sketch, "E117", {"start": v(-189.18, -141) * mm, "end": v(-184.18, -141) * mm});
            skLineSegment(sketch, "E118", {"start": v(-184.18, -141) * mm, "end": v(-184.18, -122) * mm});
            skLineSegment(sketch, "E119", {"start": v(-194.18, -142) * mm, "end": v(-189.18, -143) * mm});
            skLineSegment(sketch, "E120", {"start": v(-189.18, -143) * mm, "end": v(-189.18, -162) * mm});
            skLineSegment(sketch, "E121", {"start": v(-179.18, -142) * mm, "end": v(-184.18, -143) * mm});
            skLineSegment(sketch, "E122", {"start": v(-184.18, -143) * mm, "end": v(-184.18, -162) * mm});
            skLineSegment(sketch, "E123.bottom", {"start": v(-179.18, -249) * mm, "end": v(-194.18, -249) * mm});
            skLineSegment(sketch, "E123.top", {"start": v(-179.18, -209) * mm, "end": v(-194.18, -209) * mm});
            skLineSegment(sketch, "E123.left", {"start": v(-179.18, -249) * mm, "end": v(-179.18, -209) * mm});
            skLineSegment(sketch, "E123.right", {"start": v(-194.18, -249) * mm, "end": v(-194.18, -209) * mm});
            skPoint(sketch, "E123.middle", {"position": v(-186.68, -229) * mm});
            skLineSegment(sketch, "E124", {"start": v(-189.18, -209) * mm, "end": v(-189.18, -228) * mm});
            skLineSegment(sketch, "E125", {"start": v(-189.18, -228) * mm, "end": v(-184.18, -228) * mm});
            skLineSegment(sketch, "E126", {"start": v(-184.18, -228) * mm, "end": v(-184.18, -209) * mm});
            skLineSegment(sketch, "E127", {"start": v(-194.18, -229) * mm, "end": v(-189.18, -230) * mm});
            skLineSegment(sketch, "E128", {"start": v(-189.18, -230) * mm, "end": v(-189.18, -249) * mm});
            skLineSegment(sketch, "E129", {"start": v(-179.18, -229) * mm, "end": v(-184.18, -230) * mm});
            skLineSegment(sketch, "E130", {"start": v(-184.18, -230) * mm, "end": v(-184.18, -249) * mm});
            skSolve(sketch);
        }
        {
            var Q0;
            {var subQ4=sQuery(id+"F12.wireOp",EDGE,"E111");Q0=makeQuery(id+"F12.imprint","IMPRINT",FACE,{"disambiguationData":[TD([[makeQuery(id+"F12.imprint","IMPRINT",EDGE,{"derivedFrom":subQ4}),-1.0]])]});}
            var Q1;
            {var subQ0=sQuery(id+"F12.wireOp",EDGE,"E108");Q1=makeQuery(id+"F12.imprint","IMPRINT",FACE,{"disambiguationData":[TD([[makeQuery(id+"F12.imprint","IMPRINT",EDGE,{"derivedFrom":subQ0}),1.0]])]});}
            var Q2;
            {var subQ4=sQuery(id+"F12.wireOp",EDGE,"E113");Q2=makeQuery(id+"F12.imprint","IMPRINT",FACE,{"disambiguationData":[TD([[makeQuery(id+"F12.imprint","IMPRINT",EDGE,{"derivedFrom":subQ4}),1.0]])]});}
            var Q3;
            {var subQ0=sQuery(id+"F12.wireOp",EDGE,"E100");Q3=makeQuery(id+"F12.imprint","IMPRINT",FACE,{"disambiguationData":[TD([[makeQuery(id+"F12.imprint","IMPRINT",EDGE,{"derivedFrom":subQ0}),1.0]])]});}
            var Q4;
            {var subQ4=sQuery(id+"F12.wireOp",EDGE,"E103");Q4=makeQuery(id+"F12.imprint","IMPRINT",FACE,{"disambiguationData":[TD([[makeQuery(id+"F12.imprint","IMPRINT",EDGE,{"derivedFrom":subQ4}),-1.0]])]});}
            var Q5;
            {var subQ4=sQuery(id+"F12.wireOp",EDGE,"E105");Q5=makeQuery(id+"F12.imprint","IMPRINT",FACE,{"disambiguationData":[TD([[makeQuery(id+"F12.imprint","IMPRINT",EDGE,{"derivedFrom":subQ4}),1.0]])]});}
            var Q6;
            {var subQ0=sQuery(id+"F12.wireOp",EDGE,"E92");Q6=makeQuery(id+"F12.imprint","IMPRINT",FACE,{"disambiguationData":[TD([[makeQuery(id+"F12.imprint","IMPRINT",EDGE,{"derivedFrom":subQ0}),1.0]])]});}
            var Q7;
            {var subQ4=sQuery(id+"F12.wireOp",EDGE,"E97");Q7=makeQuery(id+"F12.imprint","IMPRINT",FACE,{"disambiguationData":[TD([[makeQuery(id+"F12.imprint","IMPRINT",EDGE,{"derivedFrom":subQ4}),1.0]])]});}
            var Q8;
            {var subQ4=sQuery(id+"F12.wireOp",EDGE,"E95");Q8=makeQuery(id+"F12.imprint","IMPRINT",FACE,{"disambiguationData":[TD([[makeQuery(id+"F12.imprint","IMPRINT",EDGE,{"derivedFrom":subQ4}),-1.0]])]});}
            var Q9;
            {var subQ0=sQuery(id+"F12.wireOp",EDGE,"E116");Q9=makeQuery(id+"F12.imprint","IMPRINT",FACE,{"disambiguationData":[TD([[makeQuery(id+"F12.imprint","IMPRINT",EDGE,{"derivedFrom":subQ0}),1.0]])]});}
            var Q10;
            {var subQ4=sQuery(id+"F12.wireOp",EDGE,"E119");Q10=makeQuery(id+"F12.imprint","IMPRINT",FACE,{"disambiguationData":[TD([[makeQuery(id+"F12.imprint","IMPRINT",EDGE,{"derivedFrom":subQ4}),-1.0]])]});}
            var Q11;
            {var subQ4=sQuery(id+"F12.wireOp",EDGE,"E121");Q11=makeQuery(id+"F12.imprint","IMPRINT",FACE,{"disambiguationData":[TD([[makeQuery(id+"F12.imprint","IMPRINT",EDGE,{"derivedFrom":subQ4}),1.0]])]});}
            var Q12;
            {var subQ0=sQuery(id+"F12.wireOp",EDGE,"E124");Q12=makeQuery(id+"F12.imprint","IMPRINT",FACE,{"disambiguationData":[TD([[makeQuery(id+"F12.imprint","IMPRINT",EDGE,{"derivedFrom":subQ0}),1.0]])]});}
            var Q13;
            {var subQ4=sQuery(id+"F12.wireOp",EDGE,"E127");Q13=makeQuery(id+"F12.imprint","IMPRINT",FACE,{"disambiguationData":[TD([[makeQuery(id+"F12.imprint","IMPRINT",EDGE,{"derivedFrom":subQ4}),-1.0]])]});}
            var Q14;
            {var subQ4=sQuery(id+"F12.wireOp",EDGE,"E129");Q14=makeQuery(id+"F12.imprint","IMPRINT",FACE,{"disambiguationData":[TD([[makeQuery(id+"F12.imprint","IMPRINT",EDGE,{"derivedFrom":subQ4}),1.0]])]});}
            extrude(context, id + "F13", {"entities" : qUnion([Q0, Q1, Q2, Q3, Q4, Q5, Q6, Q7, Q8, Q9, Q10, Q11, Q12, Q13, Q14]), "operationType" : NewBodyOperationType.REMOVE, "oppositeDirection" : true, "depth" : 15 * mm});
        }
        {
            var Q0;
            {var subQ4=sQuery(id+"F12.wireOp",EDGE,"E116");Q0=makeQuery(id+"F12.imprint","IMPRINT",FACE,{"disambiguationData":[TD([[makeQuery(id+"F12.imprint","IMPRINT",EDGE,{"derivedFrom":subQ4}),-1.0]])]});}
            var Q1;
            {var subQ1=sQuery(id+"F12.wireOp",EDGE,"E124");Q1=makeQuery(id+"F12.imprint","IMPRINT",FACE,{"disambiguationData":[TD([[makeQuery(id+"F12.imprint","IMPRINT",EDGE,{"derivedFrom":subQ1}),-1.0]])]});}
            var Q2;
            {var subQ8=sQuery(id+"F12.wireOp",EDGE,"E108");Q2=makeQuery(id+"F12.imprint","IMPRINT",FACE,{"disambiguationData":[TD([[makeQuery(id+"F12.imprint","IMPRINT",EDGE,{"derivedFrom":subQ8}),-1.0]])]});}
            var Q3;
            {var subQ1=sQuery(id+"F12.wireOp",EDGE,"E100");Q3=makeQuery(id+"F12.imprint","IMPRINT",FACE,{"disambiguationData":[TD([[makeQuery(id+"F12.imprint","IMPRINT",EDGE,{"derivedFrom":subQ1}),-1.0]])]});}
            var Q4;
            {var subQ2=sQuery(id+"F12.wireOp",EDGE,"E92");Q4=makeQuery(id+"F12.imprint","IMPRINT",FACE,{"disambiguationData":[TD([[makeQuery(id+"F12.imprint","IMPRINT",EDGE,{"derivedFrom":subQ2}),-1.0]])]});}
            extrude(context, id + "F14", {"entities" : qUnion([Q0, Q1, Q2, Q3, Q4]), "operationType" : NewBodyOperationType.ADD, "depth" : 15 * mm});
        }
        {
            var Q0;
            Q0=makeQuery(id+"F7.opChamfer","BLEND_FACE",FACE,{"disambiguationData":[OSD([sQuery(id+"F0.wireOp",EDGE,"E0.bottom")])]});
            var sketch = newSketch(context, id + "F15", { "sketchPlane" : qUnion([Q0])});
            skLineSegment(sketch, "E131", {"start": v(-257.73, -176.07) * mm, "end": v(-257.73, -197.28) * mm, "construction": true});
            skLineSegment(sketch, "E132", {"start": v(-257.73, -186.68) * mm, "end": v(262.82, -186.68) * mm, "construction": true});
            skLineSegment(sketch, "E133.bottom", {"start": v(-209, -194.18) * mm, "end": v(-249, -194.18) * mm});
            skLineSegment(sketch, "E133.top", {"start": v(-209, -179.18) * mm, "end": v(-249, -179.18) * mm});
            skLineSegment(sketch, "E133.left", {"start": v(-209, -194.18) * mm, "end": v(-209, -179.18) * mm});
            skLineSegment(sketch, "E133.right", {"start": v(-249, -194.18) * mm, "end": v(-249, -179.18) * mm});
            skPoint(sketch, "E133.middle", {"position": v(-229, -186.68) * mm});
            skLineSegment(sketch, "E134", {"start": v(-209, -184.18) * mm, "end": v(-228, -184.18) * mm});
            skLineSegment(sketch, "E135", {"start": v(-228, -189.18) * mm, "end": v(-209, -189.18) * mm});
            skLineSegment(sketch, "E136", {"start": v(-230, -189.18) * mm, "end": v(-249, -189.18) * mm});
            skLineSegment(sketch, "E137", {"start": v(-230, -184.18) * mm, "end": v(-230, -189.18) * mm});
            skLineSegment(sketch, "E138", {"start": v(-230, -184.18) * mm, "end": v(-249, -184.18) * mm});
            skLineSegment(sketch, "E139", {"start": v(-229, -179.18) * mm, "end": v(-228, -184.18) * mm});
            skLineSegment(sketch, "E140", {"start": v(-229, -194.18) * mm, "end": v(-228, -189.18) * mm});
            skLineSegment(sketch, "E141.bottom", {"start": v(-122, -194.18) * mm, "end": v(-162, -194.18) * mm});
            skLineSegment(sketch, "E141.top", {"start": v(-122, -179.18) * mm, "end": v(-162, -179.18) * mm});
            skLineSegment(sketch, "E141.left", {"start": v(-122, -194.18) * mm, "end": v(-122, -179.18) * mm});
            skLineSegment(sketch, "E141.right", {"start": v(-162, -194.18) * mm, "end": v(-162, -179.18) * mm});
            skPoint(sketch, "E141.middle", {"position": v(-142, -186.68) * mm});
            skLineSegment(sketch, "E142", {"start": v(-122, -184.18) * mm, "end": v(-141, -184.18) * mm});
            skLineSegment(sketch, "E143", {"start": v(-141, -189.18) * mm, "end": v(-122, -189.18) * mm});
            skLineSegment(sketch, "E144", {"start": v(-143, -189.18) * mm, "end": v(-162, -189.18) * mm});
            skLineSegment(sketch, "E145", {"start": v(-143, -184.18) * mm, "end": v(-143, -189.18) * mm});
            skLineSegment(sketch, "E146", {"start": v(-143, -184.18) * mm, "end": v(-162, -184.18) * mm});
            skLineSegment(sketch, "E147", {"start": v(-142, -179.18) * mm, "end": v(-141, -184.18) * mm});
            skLineSegment(sketch, "E148", {"start": v(-142, -194.18) * mm, "end": v(-141, -189.18) * mm});
            skLineSegment(sketch, "E149.bottom", {"start": v(20, -194.18) * mm, "end": v(-20, -194.18) * mm});
            skLineSegment(sketch, "E149.top", {"start": v(20, -179.18) * mm, "end": v(-20, -179.18) * mm});
            skLineSegment(sketch, "E149.left", {"start": v(20, -194.18) * mm, "end": v(20, -179.18) * mm});
            skLineSegment(sketch, "E149.right", {"start": v(-20, -194.18) * mm, "end": v(-20, -179.18) * mm});
            skPoint(sketch, "E149.middle", {"position": v(0, -186.68) * mm});
            skLineSegment(sketch, "E150", {"start": v(20, -184.18) * mm, "end": v(1, -184.18) * mm});
            skLineSegment(sketch, "E151", {"start": v(1, -189.18) * mm, "end": v(20, -189.18) * mm});
            skLineSegment(sketch, "E152", {"start": v(-1, -189.18) * mm, "end": v(-20, -189.18) * mm});
            skLineSegment(sketch, "E153", {"start": v(-1, -184.18) * mm, "end": v(-1, -189.18) * mm});
            skLineSegment(sketch, "E154", {"start": v(-1, -184.18) * mm, "end": v(-20, -184.18) * mm});
            skLineSegment(sketch, "E155", {"start": v(0, -179.18) * mm, "end": v(1, -184.18) * mm});
            skLineSegment(sketch, "E156", {"start": v(0, -194.18) * mm, "end": v(1, -189.18) * mm});
            skLineSegment(sketch, "E157.bottom", {"start": v(162, -194.18) * mm, "end": v(122, -194.18) * mm});
            skLineSegment(sketch, "E157.top", {"start": v(162, -179.18) * mm, "end": v(122, -179.18) * mm});
            skLineSegment(sketch, "E157.left", {"start": v(162, -194.18) * mm, "end": v(162, -179.18) * mm});
            skLineSegment(sketch, "E157.right", {"start": v(122, -194.18) * mm, "end": v(122, -179.18) * mm});
            skPoint(sketch, "E157.middle", {"position": v(142, -186.68) * mm});
            skLineSegment(sketch, "E158", {"start": v(162, -184.18) * mm, "end": v(143, -184.18) * mm});
            skLineSegment(sketch, "E159", {"start": v(143, -189.18) * mm, "end": v(162, -189.18) * mm});
            skLineSegment(sketch, "E160", {"start": v(141, -189.18) * mm, "end": v(122, -189.18) * mm});
            skLineSegment(sketch, "E161", {"start": v(141, -184.18) * mm, "end": v(141, -189.18) * mm});
            skLineSegment(sketch, "E162", {"start": v(141, -184.18) * mm, "end": v(122, -184.18) * mm});
            skLineSegment(sketch, "E163", {"start": v(142, -179.18) * mm, "end": v(143, -184.18) * mm});
            skLineSegment(sketch, "E164", {"start": v(142, -194.18) * mm, "end": v(143, -189.18) * mm});
            skLineSegment(sketch, "E165.bottom", {"start": v(249, -194.18) * mm, "end": v(209, -194.18) * mm});
            skLineSegment(sketch, "E165.top", {"start": v(249, -179.18) * mm, "end": v(209, -179.18) * mm});
            skLineSegment(sketch, "E165.left", {"start": v(249, -194.18) * mm, "end": v(249, -179.18) * mm});
            skLineSegment(sketch, "E165.right", {"start": v(209, -194.18) * mm, "end": v(209, -179.18) * mm});
            skPoint(sketch, "E165.middle", {"position": v(229, -186.68) * mm});
            skLineSegment(sketch, "E166", {"start": v(249, -184.18) * mm, "end": v(230, -184.18) * mm});
            skLineSegment(sketch, "E167", {"start": v(230, -189.18) * mm, "end": v(249, -189.18) * mm});
            skLineSegment(sketch, "E168", {"start": v(228, -189.18) * mm, "end": v(209, -189.18) * mm});
            skLineSegment(sketch, "E169", {"start": v(228, -184.18) * mm, "end": v(228, -189.18) * mm});
            skLineSegment(sketch, "E170", {"start": v(228, -184.18) * mm, "end": v(209, -184.18) * mm});
            skLineSegment(sketch, "E171", {"start": v(229, -179.18) * mm, "end": v(230, -184.18) * mm});
            skLineSegment(sketch, "E172", {"start": v(229, -194.18) * mm, "end": v(230, -189.18) * mm});
            skSolve(sketch);
        }
        {
            var Q0;
            {var subQ0=sQuery(id+"F15.wireOp",EDGE,"E136");Q0=makeQuery(id+"F15.imprint","IMPRINT",FACE,{"disambiguationData":[TD([[makeQuery(id+"F15.imprint","IMPRINT",EDGE,{"derivedFrom":subQ0}),-1.0]])]});}
            var Q1;
            {var subQ4=sQuery(id+"F15.wireOp",EDGE,"E134");Q1=makeQuery(id+"F15.imprint","IMPRINT",FACE,{"disambiguationData":[TD([[makeQuery(id+"F15.imprint","IMPRINT",EDGE,{"derivedFrom":subQ4}),-1.0]])]});}
            var Q2;
            {var subQ4=sQuery(id+"F15.wireOp",EDGE,"E135");Q2=makeQuery(id+"F15.imprint","IMPRINT",FACE,{"disambiguationData":[TD([[makeQuery(id+"F15.imprint","IMPRINT",EDGE,{"derivedFrom":subQ4}),-1.0]])]});}
            var Q3;
            {var subQ0=sQuery(id+"F15.wireOp",EDGE,"E144");Q3=makeQuery(id+"F15.imprint","IMPRINT",FACE,{"disambiguationData":[TD([[makeQuery(id+"F15.imprint","IMPRINT",EDGE,{"derivedFrom":subQ0}),-1.0]])]});}
            var Q4;
            {var subQ4=sQuery(id+"F15.wireOp",EDGE,"E142");Q4=makeQuery(id+"F15.imprint","IMPRINT",FACE,{"disambiguationData":[TD([[makeQuery(id+"F15.imprint","IMPRINT",EDGE,{"derivedFrom":subQ4}),-1.0]])]});}
            var Q5;
            {var subQ4=sQuery(id+"F15.wireOp",EDGE,"E143");Q5=makeQuery(id+"F15.imprint","IMPRINT",FACE,{"disambiguationData":[TD([[makeQuery(id+"F15.imprint","IMPRINT",EDGE,{"derivedFrom":subQ4}),-1.0]])]});}
            var Q6;
            {var subQ0=sQuery(id+"F15.wireOp",EDGE,"E152");Q6=makeQuery(id+"F15.imprint","IMPRINT",FACE,{"disambiguationData":[TD([[makeQuery(id+"F15.imprint","IMPRINT",EDGE,{"derivedFrom":subQ0}),-1.0]])]});}
            var Q7;
            {var subQ4=sQuery(id+"F15.wireOp",EDGE,"E150");Q7=makeQuery(id+"F15.imprint","IMPRINT",FACE,{"disambiguationData":[TD([[makeQuery(id+"F15.imprint","IMPRINT",EDGE,{"derivedFrom":subQ4}),-1.0]])]});}
            var Q8;
            {var subQ4=sQuery(id+"F15.wireOp",EDGE,"E151");Q8=makeQuery(id+"F15.imprint","IMPRINT",FACE,{"disambiguationData":[TD([[makeQuery(id+"F15.imprint","IMPRINT",EDGE,{"derivedFrom":subQ4}),-1.0]])]});}
            var Q9;
            {var subQ0=sQuery(id+"F15.wireOp",EDGE,"E160");Q9=makeQuery(id+"F15.imprint","IMPRINT",FACE,{"disambiguationData":[TD([[makeQuery(id+"F15.imprint","IMPRINT",EDGE,{"derivedFrom":subQ0}),-1.0]])]});}
            var Q10;
            {var subQ4=sQuery(id+"F15.wireOp",EDGE,"E158");Q10=makeQuery(id+"F15.imprint","IMPRINT",FACE,{"disambiguationData":[TD([[makeQuery(id+"F15.imprint","IMPRINT",EDGE,{"derivedFrom":subQ4}),-1.0]])]});}
            var Q11;
            {var subQ4=sQuery(id+"F15.wireOp",EDGE,"E159");Q11=makeQuery(id+"F15.imprint","IMPRINT",FACE,{"disambiguationData":[TD([[makeQuery(id+"F15.imprint","IMPRINT",EDGE,{"derivedFrom":subQ4}),-1.0]])]});}
            var Q12;
            {var subQ0=sQuery(id+"F15.wireOp",EDGE,"E168");Q12=makeQuery(id+"F15.imprint","IMPRINT",FACE,{"disambiguationData":[TD([[makeQuery(id+"F15.imprint","IMPRINT",EDGE,{"derivedFrom":subQ0}),-1.0]])]});}
            var Q13;
            {var subQ4=sQuery(id+"F15.wireOp",EDGE,"E166");Q13=makeQuery(id+"F15.imprint","IMPRINT",FACE,{"disambiguationData":[TD([[makeQuery(id+"F15.imprint","IMPRINT",EDGE,{"derivedFrom":subQ4}),-1.0]])]});}
            var Q14;
            {var subQ4=sQuery(id+"F15.wireOp",EDGE,"E167");Q14=makeQuery(id+"F15.imprint","IMPRINT",FACE,{"disambiguationData":[TD([[makeQuery(id+"F15.imprint","IMPRINT",EDGE,{"derivedFrom":subQ4}),-1.0]])]});}
            extrude(context, id + "F16", {"entities" : qUnion([Q0, Q1, Q2, Q3, Q4, Q5, Q6, Q7, Q8, Q9, Q10, Q11, Q12, Q13, Q14]), "operationType" : NewBodyOperationType.REMOVE, "oppositeDirection" : true, "depth" : 15 * mm});
        }
        {
            var Q0;
            {var subQ5=sQuery(id+"F15.wireOp",EDGE,"E134");Q0=makeQuery(id+"F15.imprint","IMPRINT",FACE,{"disambiguationData":[TD([[makeQuery(id+"F15.imprint","IMPRINT",EDGE,{"derivedFrom":subQ5}),1.0]])]});}
            var Q1;
            {var subQ7=sQuery(id+"F15.wireOp",EDGE,"E142");Q1=makeQuery(id+"F15.imprint","IMPRINT",FACE,{"disambiguationData":[TD([[makeQuery(id+"F15.imprint","IMPRINT",EDGE,{"derivedFrom":subQ7}),1.0]])]});}
            var Q2;
            {var subQ0=sQuery(id+"F15.wireOp",EDGE,"E150");Q2=makeQuery(id+"F15.imprint","IMPRINT",FACE,{"disambiguationData":[TD([[makeQuery(id+"F15.imprint","IMPRINT",EDGE,{"derivedFrom":subQ0}),1.0]])]});}
            var Q3;
            {var subQ2=sQuery(id+"F15.wireOp",EDGE,"E158");Q3=makeQuery(id+"F15.imprint","IMPRINT",FACE,{"disambiguationData":[TD([[makeQuery(id+"F15.imprint","IMPRINT",EDGE,{"derivedFrom":subQ2}),1.0]])]});}
            var Q4;
            {var subQ5=sQuery(id+"F15.wireOp",EDGE,"E166");Q4=makeQuery(id+"F15.imprint","IMPRINT",FACE,{"disambiguationData":[TD([[makeQuery(id+"F15.imprint","IMPRINT",EDGE,{"derivedFrom":subQ5}),1.0]])]});}
            extrude(context, id + "F17", {"entities" : qUnion([Q0, Q1, Q2, Q3, Q4]), "operationType" : NewBodyOperationType.ADD, "depth" : 15 * mm});
        }
        {
            var Q0;
            Q0=makeQuery(id+"F7.opChamfer","BLEND_FACE",FACE,{"disambiguationData":[OSD([sQuery(id+"F0.wireOp",EDGE,"E0.top")])]});
            var sketch = newSketch(context, id + "F18", { "sketchPlane" : qUnion([Q0])});
            skLineSegment(sketch, "E173.bottom", {"start": v(-209, 179.18) * mm, "end": v(-249, 179.18) * mm});
            skLineSegment(sketch, "E173.top", {"start": v(-209, 194.18) * mm, "end": v(-249, 194.18) * mm});
            skLineSegment(sketch, "E173.left", {"start": v(-209, 179.18) * mm, "end": v(-209, 194.18) * mm});
            skLineSegment(sketch, "E173.right", {"start": v(-249, 179.18) * mm, "end": v(-249, 194.18) * mm});
            skPoint(sketch, "E173.middle", {"position": v(-229, 186.68) * mm});
            skLineSegment(sketch, "E174", {"start": v(-209, 189.18) * mm, "end": v(-228, 189.18) * mm});
            skLineSegment(sketch, "E175", {"start": v(-228, 189.18) * mm, "end": v(-228, 184.18) * mm});
            skLineSegment(sketch, "E176", {"start": v(-228, 184.18) * mm, "end": v(-209, 184.18) * mm});
            skLineSegment(sketch, "E177", {"start": v(-249, 189.18) * mm, "end": v(-230, 189.18) * mm});
            skLineSegment(sketch, "E178", {"start": v(-230, 189.18) * mm, "end": v(-229, 194.18) * mm});
            skLineSegment(sketch, "E179", {"start": v(-229, 179.18) * mm, "end": v(-230, 184.18) * mm});
            skLineSegment(sketch, "E180", {"start": v(-230, 184.18) * mm, "end": v(-249, 184.18) * mm});
            skLineSegment(sketch, "E181.bottom", {"start": v(-122, 179.18) * mm, "end": v(-162, 179.18) * mm});
            skLineSegment(sketch, "E181.top", {"start": v(-122, 194.18) * mm, "end": v(-162, 194.18) * mm});
            skLineSegment(sketch, "E181.left", {"start": v(-122, 179.18) * mm, "end": v(-122, 194.18) * mm});
            skLineSegment(sketch, "E181.right", {"start": v(-162, 179.18) * mm, "end": v(-162, 194.18) * mm});
            skPoint(sketch, "E181.middle", {"position": v(-142, 186.68) * mm});
            skLineSegment(sketch, "E182", {"start": v(-122, 189.18) * mm, "end": v(-141, 189.18) * mm});
            skLineSegment(sketch, "E183", {"start": v(-141, 189.18) * mm, "end": v(-141, 184.18) * mm});
            skLineSegment(sketch, "E184", {"start": v(-141, 184.18) * mm, "end": v(-122, 184.18) * mm});
            skLineSegment(sketch, "E185", {"start": v(-162, 189.18) * mm, "end": v(-143, 189.18) * mm});
            skLineSegment(sketch, "E186", {"start": v(-143, 189.18) * mm, "end": v(-142, 194.18) * mm});
            skLineSegment(sketch, "E187", {"start": v(-142, 179.18) * mm, "end": v(-143, 184.18) * mm});
            skLineSegment(sketch, "E188", {"start": v(-143, 184.18) * mm, "end": v(-162, 184.18) * mm});
            skLineSegment(sketch, "E189.bottom", {"start": v(20, 179.18) * mm, "end": v(-20, 179.18) * mm});
            skLineSegment(sketch, "E189.top", {"start": v(20, 194.18) * mm, "end": v(-20, 194.18) * mm});
            skLineSegment(sketch, "E189.left", {"start": v(20, 179.18) * mm, "end": v(20, 194.18) * mm});
            skLineSegment(sketch, "E189.right", {"start": v(-20, 179.18) * mm, "end": v(-20, 194.18) * mm});
            skPoint(sketch, "E189.middle", {"position": v(0, 186.68) * mm});
            skLineSegment(sketch, "E190", {"start": v(20, 189.18) * mm, "end": v(1, 189.18) * mm});
            skLineSegment(sketch, "E191", {"start": v(1, 189.18) * mm, "end": v(1, 184.18) * mm});
            skLineSegment(sketch, "E192", {"start": v(1, 184.18) * mm, "end": v(20, 184.18) * mm});
            skLineSegment(sketch, "E193", {"start": v(-20, 189.18) * mm, "end": v(-1, 189.18) * mm});
            skLineSegment(sketch, "E194", {"start": v(-1, 189.18) * mm, "end": v(0, 194.18) * mm});
            skLineSegment(sketch, "E195", {"start": v(0, 179.18) * mm, "end": v(-1, 184.18) * mm});
            skLineSegment(sketch, "E196", {"start": v(-1, 184.18) * mm, "end": v(-20, 184.18) * mm});
            skLineSegment(sketch, "E197.bottom", {"start": v(162, 179.18) * mm, "end": v(122, 179.18) * mm});
            skLineSegment(sketch, "E197.top", {"start": v(162, 194.18) * mm, "end": v(122, 194.18) * mm});
            skLineSegment(sketch, "E197.left", {"start": v(162, 179.18) * mm, "end": v(162, 194.18) * mm});
            skLineSegment(sketch, "E197.right", {"start": v(122, 179.18) * mm, "end": v(122, 194.18) * mm});
            skPoint(sketch, "E197.middle", {"position": v(142, 186.68) * mm});
            skLineSegment(sketch, "E198", {"start": v(162, 189.18) * mm, "end": v(143, 189.18) * mm});
            skLineSegment(sketch, "E199", {"start": v(143, 189.18) * mm, "end": v(143, 184.18) * mm});
            skLineSegment(sketch, "E200", {"start": v(143, 184.18) * mm, "end": v(162, 184.18) * mm});
            skLineSegment(sketch, "E201", {"start": v(122, 189.18) * mm, "end": v(141, 189.18) * mm});
            skLineSegment(sketch, "E202", {"start": v(141, 189.18) * mm, "end": v(142, 194.18) * mm});
            skLineSegment(sketch, "E203", {"start": v(142, 179.18) * mm, "end": v(141, 184.18) * mm});
            skLineSegment(sketch, "E204", {"start": v(141, 184.18) * mm, "end": v(122, 184.18) * mm});
            skLineSegment(sketch, "E205.bottom", {"start": v(249, 179.18) * mm, "end": v(209, 179.18) * mm});
            skLineSegment(sketch, "E205.top", {"start": v(249, 194.18) * mm, "end": v(209, 194.18) * mm});
            skLineSegment(sketch, "E205.left", {"start": v(249, 179.18) * mm, "end": v(249, 194.18) * mm});
            skLineSegment(sketch, "E205.right", {"start": v(209, 179.18) * mm, "end": v(209, 194.18) * mm});
            skPoint(sketch, "E205.middle", {"position": v(229, 186.68) * mm});
            skLineSegment(sketch, "E206", {"start": v(249, 189.18) * mm, "end": v(230, 189.18) * mm});
            skLineSegment(sketch, "E207", {"start": v(230, 189.18) * mm, "end": v(230, 184.18) * mm});
            skLineSegment(sketch, "E208", {"start": v(230, 184.18) * mm, "end": v(249, 184.18) * mm});
            skLineSegment(sketch, "E209", {"start": v(209, 189.18) * mm, "end": v(228, 189.18) * mm});
            skLineSegment(sketch, "E210", {"start": v(228, 189.18) * mm, "end": v(229, 194.18) * mm});
            skLineSegment(sketch, "E211", {"start": v(229, 179.18) * mm, "end": v(228, 184.18) * mm});
            skLineSegment(sketch, "E212", {"start": v(228, 184.18) * mm, "end": v(209, 184.18) * mm});
            skLineSegment(sketch, "E213", {"start": v(-252.31, 197.28) * mm, "end": v(-252.31, 176.07) * mm, "construction": true});
            skLineSegment(sketch, "E214", {"start": v(-252.31, 186.68) * mm, "end": v(256.2, 186.68) * mm, "construction": true});
            skSolve(sketch);
        }
        {
            var Q0;
            {var subQ2=sQuery(id+"F18.wireOp",EDGE,"E174");Q0=makeQuery(id+"F18.imprint","IMPRINT",FACE,{"disambiguationData":[TD([[makeQuery(id+"F18.imprint","IMPRINT",EDGE,{"derivedFrom":subQ2}),-1.0]])]});}
            var Q1;
            {var subQ3=sQuery(id+"F18.wireOp",EDGE,"E182");Q1=makeQuery(id+"F18.imprint","IMPRINT",FACE,{"disambiguationData":[TD([[makeQuery(id+"F18.imprint","IMPRINT",EDGE,{"derivedFrom":subQ3}),-1.0]])]});}
            var Q2;
            {var subQ2=sQuery(id+"F18.wireOp",EDGE,"E190");Q2=makeQuery(id+"F18.imprint","IMPRINT",FACE,{"disambiguationData":[TD([[makeQuery(id+"F18.imprint","IMPRINT",EDGE,{"derivedFrom":subQ2}),-1.0]])]});}
            var Q3;
            {var subQ1=sQuery(id+"F18.wireOp",EDGE,"E198");Q3=makeQuery(id+"F18.imprint","IMPRINT",FACE,{"disambiguationData":[TD([[makeQuery(id+"F18.imprint","IMPRINT",EDGE,{"derivedFrom":subQ1}),-1.0]])]});}
            var Q4;
            {var subQ1=sQuery(id+"F18.wireOp",EDGE,"E206");Q4=makeQuery(id+"F18.imprint","IMPRINT",FACE,{"disambiguationData":[TD([[makeQuery(id+"F18.imprint","IMPRINT",EDGE,{"derivedFrom":subQ1}),-1.0]])]});}
            extrude(context, id + "F19", {"entities" : qUnion([Q0, Q1, Q2, Q3, Q4]), "operationType" : NewBodyOperationType.ADD, "depth" : 15 * mm});
        }
        {
            var Q0;
            {var subQ0=sQuery(id+"F18.wireOp",EDGE,"E206");Q0=makeQuery(id+"F18.imprint","IMPRINT",FACE,{"disambiguationData":[TD([[makeQuery(id+"F18.imprint","IMPRINT",EDGE,{"derivedFrom":subQ0}),1.0]])]});}
            var Q1;
            {var subQ4=sQuery(id+"F18.wireOp",EDGE,"E209");Q1=makeQuery(id+"F18.imprint","IMPRINT",FACE,{"disambiguationData":[TD([[makeQuery(id+"F18.imprint","IMPRINT",EDGE,{"derivedFrom":subQ4}),1.0]])]});}
            var Q2;
            {var subQ3=sQuery(id+"F18.wireOp",EDGE,"E211");Q2=makeQuery(id+"F18.imprint","IMPRINT",FACE,{"disambiguationData":[TD([[makeQuery(id+"F18.imprint","IMPRINT",EDGE,{"derivedFrom":subQ3}),1.0]])]});}
            var Q3;
            {var subQ0=sQuery(id+"F18.wireOp",EDGE,"E198");Q3=makeQuery(id+"F18.imprint","IMPRINT",FACE,{"disambiguationData":[TD([[makeQuery(id+"F18.imprint","IMPRINT",EDGE,{"derivedFrom":subQ0}),1.0]])]});}
            var Q4;
            {var subQ4=sQuery(id+"F18.wireOp",EDGE,"E201");Q4=makeQuery(id+"F18.imprint","IMPRINT",FACE,{"disambiguationData":[TD([[makeQuery(id+"F18.imprint","IMPRINT",EDGE,{"derivedFrom":subQ4}),1.0]])]});}
            var Q5;
            {var subQ3=sQuery(id+"F18.wireOp",EDGE,"E203");Q5=makeQuery(id+"F18.imprint","IMPRINT",FACE,{"disambiguationData":[TD([[makeQuery(id+"F18.imprint","IMPRINT",EDGE,{"derivedFrom":subQ3}),1.0]])]});}
            var Q6;
            {var subQ0=sQuery(id+"F18.wireOp",EDGE,"E190");Q6=makeQuery(id+"F18.imprint","IMPRINT",FACE,{"disambiguationData":[TD([[makeQuery(id+"F18.imprint","IMPRINT",EDGE,{"derivedFrom":subQ0}),1.0]])]});}
            var Q7;
            {var subQ4=sQuery(id+"F18.wireOp",EDGE,"E193");Q7=makeQuery(id+"F18.imprint","IMPRINT",FACE,{"disambiguationData":[TD([[makeQuery(id+"F18.imprint","IMPRINT",EDGE,{"derivedFrom":subQ4}),1.0]])]});}
            var Q8;
            {var subQ3=sQuery(id+"F18.wireOp",EDGE,"E195");Q8=makeQuery(id+"F18.imprint","IMPRINT",FACE,{"disambiguationData":[TD([[makeQuery(id+"F18.imprint","IMPRINT",EDGE,{"derivedFrom":subQ3}),1.0]])]});}
            var Q9;
            {var subQ0=sQuery(id+"F18.wireOp",EDGE,"E182");Q9=makeQuery(id+"F18.imprint","IMPRINT",FACE,{"disambiguationData":[TD([[makeQuery(id+"F18.imprint","IMPRINT",EDGE,{"derivedFrom":subQ0}),1.0]])]});}
            var Q10;
            {var subQ4=sQuery(id+"F18.wireOp",EDGE,"E185");Q10=makeQuery(id+"F18.imprint","IMPRINT",FACE,{"disambiguationData":[TD([[makeQuery(id+"F18.imprint","IMPRINT",EDGE,{"derivedFrom":subQ4}),1.0]])]});}
            var Q11;
            {var subQ3=sQuery(id+"F18.wireOp",EDGE,"E187");Q11=makeQuery(id+"F18.imprint","IMPRINT",FACE,{"disambiguationData":[TD([[makeQuery(id+"F18.imprint","IMPRINT",EDGE,{"derivedFrom":subQ3}),1.0]])]});}
            var Q12;
            {var subQ0=sQuery(id+"F18.wireOp",EDGE,"E174");Q12=makeQuery(id+"F18.imprint","IMPRINT",FACE,{"disambiguationData":[TD([[makeQuery(id+"F18.imprint","IMPRINT",EDGE,{"derivedFrom":subQ0}),1.0]])]});}
            var Q13;
            {var subQ4=sQuery(id+"F18.wireOp",EDGE,"E177");Q13=makeQuery(id+"F18.imprint","IMPRINT",FACE,{"disambiguationData":[TD([[makeQuery(id+"F18.imprint","IMPRINT",EDGE,{"derivedFrom":subQ4}),1.0]])]});}
            var Q14;
            {var subQ3=sQuery(id+"F18.wireOp",EDGE,"E179");Q14=makeQuery(id+"F18.imprint","IMPRINT",FACE,{"disambiguationData":[TD([[makeQuery(id+"F18.imprint","IMPRINT",EDGE,{"derivedFrom":subQ3}),1.0]])]});}
            extrude(context, id + "F20", {"entities" : qUnion([Q0, Q1, Q2, Q3, Q4, Q5, Q6, Q7, Q8, Q9, Q10, Q11, Q12, Q13, Q14]), "operationType" : NewBodyOperationType.REMOVE, "oppositeDirection" : true, "depth" : 15 * mm});
        }
        {
            var Q0;
            Q0=makeQuery(id+"F1.opExtrude","CAP_FACE",FACE,{"disambiguationData":[OSD([sQuery(id+"F0.wireOp",EDGE,"E0.bottom"),sQuery(id+"F0.wireOp",EDGE,"E0.top"),sQuery(id+"F0.wireOp",EDGE,"E0.left"),sQuery(id+"F0.wireOp",EDGE,"E0.right")])],"isStart":false});
            var sketch = newSketch(context, id + "F21", { "sketchPlane" : qUnion([Q0])});
            skLineSegment(sketch, "E215", {"start": v(-264, 264) * mm, "end": v(-264, 239) * mm, "construction": true});
            skLineSegment(sketch, "E216", {"start": v(-264, 239) * mm, "end": v(-239, 239) * mm, "construction": true});
            skCircle(sketch, "E217", {"center": v(-239, 239) * mm, "radius": 12.5 * mm});
            skLineSegment(sketch, "E218", {"start": v(239, 264) * mm, "end": v(239, 239) * mm, "construction": true});
            skCircle(sketch, "E219", {"center": v(239, 239) * mm, "radius": 12.5 * mm});
            skArc(sketch, "E220", {"start": v(239, 245.25) * mm, "mid": v(232.75, 239) * mm, "end": v(239, 232.75) * mm});
            skLineSegment(sketch, "E221", {"start": v(239, 251.5) * mm, "end": v(239, 245.25) * mm});
            skLineSegment(sketch, "E222", {"start": v(239, 232.75) * mm, "end": v(239, 226.5) * mm});
            skLineSegment(sketch, "E223", {"start": v(264, -264) * mm, "end": v(264, -239) * mm, "construction": true});
            skLineSegment(sketch, "E224", {"start": v(264, -239) * mm, "end": v(239, -239) * mm, "construction": true});
            skCircle(sketch, "E225", {"center": v(239, -239) * mm, "radius": 12.5 * mm});
            skArc(sketch, "E226", {"start": v(245.25, -239) * mm, "mid": v(239, -232.75) * mm, "end": v(232.75, -239) * mm});
            skLineSegment(sketch, "E227", {"start": v(251.5, -239) * mm, "end": v(245.25, -239) * mm});
            skLineSegment(sketch, "E228", {"start": v(232.75, -239) * mm, "end": v(226.5, -239) * mm});
            skLineSegment(sketch, "E229", {"start": v(-264, -264) * mm, "end": v(-239, -264) * mm, "construction": true});
            skLineSegment(sketch, "E230", {"start": v(-239, -264) * mm, "end": v(-239, -239) * mm, "construction": true});
            skCircle(sketch, "E231", {"center": v(-239, -239) * mm, "radius": 12.5 * mm});
            skArc(sketch, "E232", {"start": v(-239, -245.25) * mm, "mid": v(-232.75, -239) * mm, "end": v(-239, -232.75) * mm});
            skLineSegment(sketch, "E233", {"start": v(-239, -245.25) * mm, "end": v(-239, -251.5) * mm});
            skLineSegment(sketch, "E234", {"start": v(-239, -232.75) * mm, "end": v(-239, -226.5) * mm});
            skArc(sketch, "E235", {"start": v(-245.25, 239) * mm, "mid": v(-239, 232.75) * mm, "end": v(-232.75, 239) * mm});
            skLineSegment(sketch, "E236", {"start": v(-245.25, 239) * mm, "end": v(-251.5, 239) * mm});
            skLineSegment(sketch, "E237", {"start": v(-232.75, 239) * mm, "end": v(-226.5, 239) * mm});
            skSolve(sketch);
        }
        {
            var Q0;
            Q0=makeQuery(id+"F21.imprint","IMPRINT",FACE,{"disambiguationData":[TD([[makeQuery(id+"F21.imprint","IMPRINT",EDGE,{"derivedFrom":sQuery(id+"F21.wireOp",EDGE,"E217")}),1.0]])]});
            var Q1;
            Q1=makeQuery(id+"F21.imprint","IMPRINT",FACE,{"disambiguationData":[TD([[makeQuery(id+"F21.imprint","IMPRINT",EDGE,{"derivedFrom":sQuery(id+"F21.wireOp",EDGE,"StziIoPQ-sY1L-NRo0-XJdT-FhAA7d0wfem7")}),1.0]])]});
            var Q2;
            Q2=makeQuery(id+"F21.imprint","IMPRINT",FACE,{"disambiguationData":[TD([[makeQuery(id+"F21.imprint","IMPRINT",EDGE,{"derivedFrom":sQuery(id+"F21.wireOp",EDGE,"E220")}),1.0]])]});
            var Q3;
            Q3=makeQuery(id+"F21.imprint","IMPRINT",FACE,{"disambiguationData":[TD([[makeQuery(id+"F21.imprint","IMPRINT",EDGE,{"derivedFrom":sQuery(id+"F21.wireOp",EDGE,"E220")}),-1.0]])]});
            var Q4;
            Q4=makeQuery(id+"F21.imprint","IMPRINT",FACE,{"disambiguationData":[TD([[makeQuery(id+"F21.imprint","IMPRINT",EDGE,{"derivedFrom":sQuery(id+"F21.wireOp",EDGE,"E226")}),1.0]])]});
            var Q5;
            Q5=makeQuery(id+"F21.imprint","IMPRINT",FACE,{"disambiguationData":[TD([[makeQuery(id+"F21.imprint","IMPRINT",EDGE,{"derivedFrom":sQuery(id+"F21.wireOp",EDGE,"E226")}),-1.0]])]});
            var Q6;
            Q6=makeQuery(id+"F21.imprint","IMPRINT",FACE,{"disambiguationData":[TD([[makeQuery(id+"F21.imprint","IMPRINT",EDGE,{"derivedFrom":sQuery(id+"F21.wireOp",EDGE,"wkqirlst-2GO6-BLPj-pm0h-Sna4hlOtwhSZ")}),-1.0]])]});
            var Q7;
            Q7=makeQuery(id+"F21.imprint","IMPRINT",FACE,{"disambiguationData":[TD([[makeQuery(id+"F21.imprint","IMPRINT",EDGE,{"derivedFrom":sQuery(id+"F21.wireOp",EDGE,"wkqirlst-2GO6-BLPj-pm0h-Sna4hlOtwhSZ")}),1.0]])]});
            var Q8;
            Q8=makeQuery(id+"F21.imprint","IMPRINT",FACE,{"disambiguationData":[TD([[makeQuery(id+"F21.imprint","IMPRINT",EDGE,{"derivedFrom":sQuery(id+"F21.wireOp",EDGE,"E232")}),1.0]])]});
            var Q9;
            Q9=makeQuery(id+"F21.imprint","IMPRINT",FACE,{"disambiguationData":[TD([[makeQuery(id+"F21.imprint","IMPRINT",EDGE,{"derivedFrom":sQuery(id+"F21.wireOp",EDGE,"E232")}),-1.0]])]});
            extrude(context, id + "F22", {"entities" : qUnion([Q0, Q1, Q2, Q3, Q4, Q5, Q6, Q7, Q8, Q9]), "operationType" : NewBodyOperationType.REMOVE, "oppositeDirection" : true, "depth" : 20 * mm});
        }
        {
            var Q0;
            Q0=makeQuery(id+"F21.imprint","IMPRINT",FACE,{"disambiguationData":[TD([[makeQuery(id+"F21.imprint","IMPRINT",EDGE,{"derivedFrom":sQuery(id+"F21.wireOp",EDGE,"StziIoPQ-sY1L-NRo0-XJdT-FhAA7d0wfem7")}),-1.0]])]});
            var Q1;
            Q1=makeQuery(id+"F21.imprint","IMPRINT",FACE,{"disambiguationData":[TD([[makeQuery(id+"F21.imprint","IMPRINT",EDGE,{"derivedFrom":sQuery(id+"F21.wireOp",EDGE,"E220")}),-1.0]])]});
            var Q2;
            Q2=makeQuery(id+"F21.imprint","IMPRINT",FACE,{"disambiguationData":[TD([[makeQuery(id+"F21.imprint","IMPRINT",EDGE,{"derivedFrom":sQuery(id+"F21.wireOp",EDGE,"E226")}),-1.0]])]});
            var Q3;
            Q3=makeQuery(id+"F21.imprint","IMPRINT",FACE,{"disambiguationData":[TD([[makeQuery(id+"F21.imprint","IMPRINT",EDGE,{"derivedFrom":sQuery(id+"F21.wireOp",EDGE,"wkqirlst-2GO6-BLPj-pm0h-Sna4hlOtwhSZ")}),1.0]])]});
            var Q4;
            Q4=makeQuery(id+"F21.imprint","IMPRINT",FACE,{"disambiguationData":[TD([[makeQuery(id+"F21.imprint","IMPRINT",EDGE,{"derivedFrom":sQuery(id+"F21.wireOp",EDGE,"E232")}),-1.0]])]});
            var Q5;
            Q5=makeQuery(id+"F21.imprint","IMPRINT",FACE,{"disambiguationData":[TD([[makeQuery(id+"F21.imprint","IMPRINT",EDGE,{"derivedFrom":sQuery(id+"F21.wireOp",EDGE,"E235")}),-1.0]])]});
            extrude(context, id + "F23", {"entities" : qUnion([Q0, Q1, Q2, Q3, Q4, Q5]), "operationType" : NewBodyOperationType.ADD, "oppositeDirection" : true, "depth" : 15 * mm});
        }
        {
            var Q0;
            Q0=makeQuery(id+"F23.opExtrude","CAP_EDGE",EDGE,{"disambiguationData":[OSD([sQuery(id+"F21.wireOp",EDGE,"E220")])],"isStart":false});
            var Q1;
            Q1=makeQuery(id+"F23.opExtrude","CAP_EDGE",EDGE,{"disambiguationData":[OSD([sQuery(id+"F21.wireOp",EDGE,"E235")])],"isStart":false});
            var Q2;
            Q2=makeQuery(id+"F23.opExtrude","CAP_EDGE",EDGE,{"disambiguationData":[OSD([sQuery(id+"F21.wireOp",EDGE,"E232")])],"isStart":false});
            var Q3;
            Q3=makeQuery(id+"F23.opExtrude","CAP_EDGE",EDGE,{"disambiguationData":[OSD([sQuery(id+"F21.wireOp",EDGE,"E226")])],"isStart":false});
            chamfer(context, id + "F24", {"entities" : qUnion([Q0, Q1, Q2, Q3]), "width" : 6.25 * mm, "tangentPropagation" : true});
        }
    });
